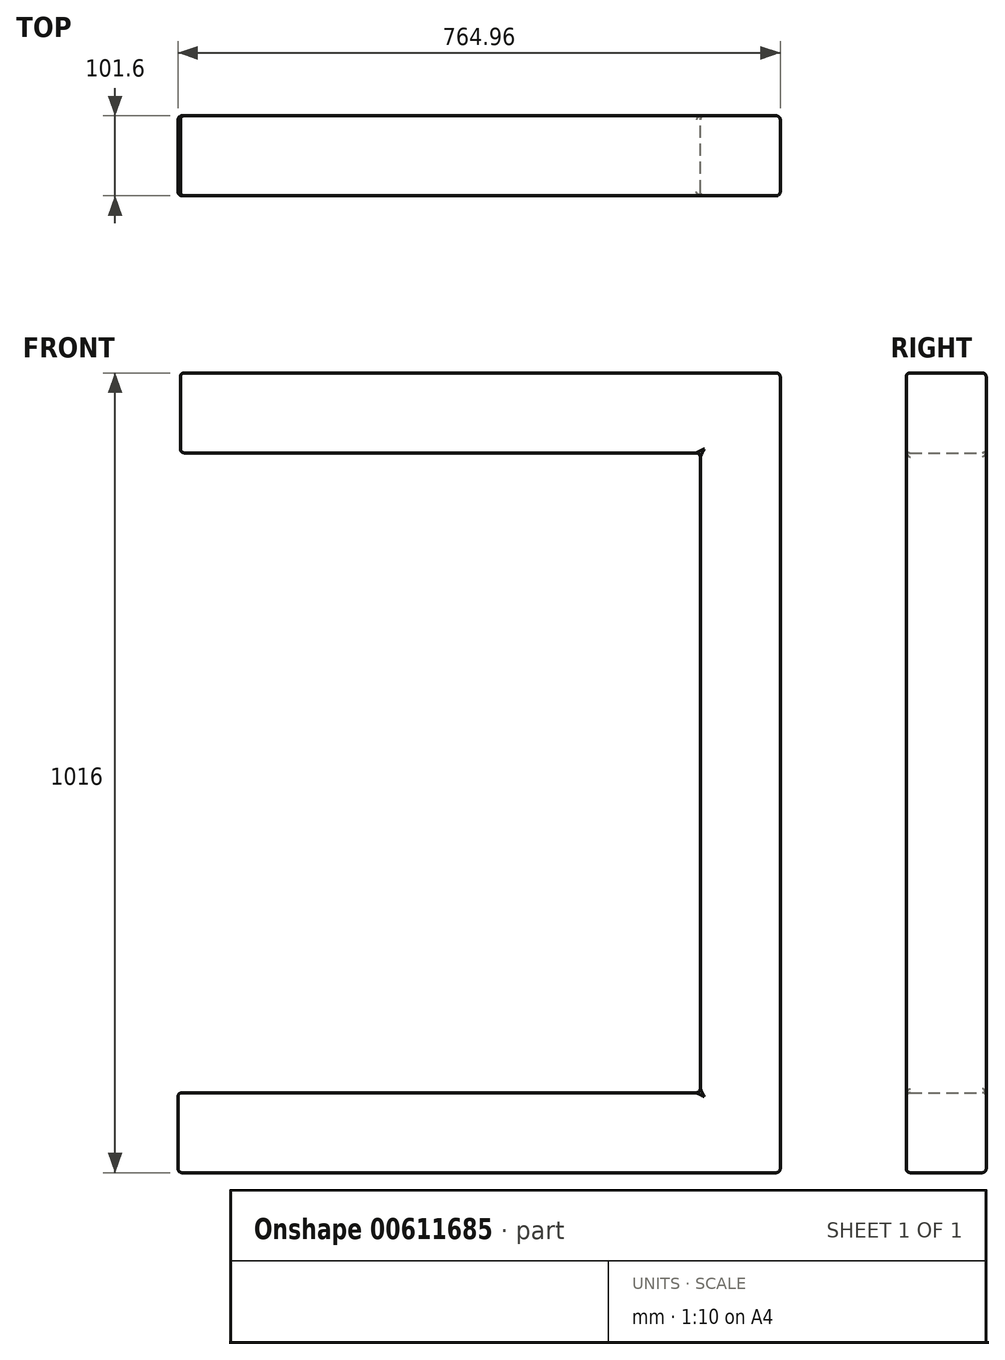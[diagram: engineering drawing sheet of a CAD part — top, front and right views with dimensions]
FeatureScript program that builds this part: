
annotation { "Feature Type Name" : "Feature", "Feature Type Description" : "" }
export const myFeature = defineFeature(function(context is Context, id is Id, definition is map)
    precondition{}
    {
        {
            var Q0;
            Q0=qCreatedBy(makeId("Front.planeOp"),FACE);
            var sketch = newSketch(context, id + "F0", { "sketchPlane" : qUnion([Q0])});
            skLineSegment(sketch, "E0.bottom", {"start": v(-441.4, 413.34) * mm, "end": v(219, 413.34) * mm});
            skLineSegment(sketch, "E0.top", {"start": v(-441.4, 311.74) * mm, "end": v(219, 311.74) * mm});
            skLineSegment(sketch, "E0.left", {"start": v(-441.4, 413.34) * mm, "end": v(-441.4, 311.74) * mm});
            skLineSegment(sketch, "E0.right", {"start": v(219, 413.34) * mm, "end": v(219, 311.74) * mm});
            skLineSegment(sketch, "E1.bottom", {"start": v(219, 413.34) * mm, "end": v(320.6, 413.34) * mm});
            skLineSegment(sketch, "E1.top", {"start": v(219, -602.66) * mm, "end": v(320.6, -602.66) * mm});
            skLineSegment(sketch, "E1.left", {"start": v(219, 413.34) * mm, "end": v(219, -602.66) * mm});
            skLineSegment(sketch, "E1.right", {"start": v(320.6, 413.34) * mm, "end": v(320.6, -602.66) * mm});
            skLineSegment(sketch, "E2.bottom", {"start": v(-444.37, -501.06) * mm, "end": v(219, -501.06) * mm});
            skLineSegment(sketch, "E2.top", {"start": v(-444.37, -602.66) * mm, "end": v(219, -602.66) * mm});
            skLineSegment(sketch, "E2.left", {"start": v(-444.37, -501.06) * mm, "end": v(-444.37, -602.66) * mm});
            skLineSegment(sketch, "E2.right", {"start": v(219, -501.06) * mm, "end": v(219, -602.66) * mm});
            skSolve(sketch);
        }
        {
            var Q0;
            Q0=makeQuery(id+"F0.imprint","IMPRINT",FACE,{"disambiguationData":[TD([[makeQuery(id+"F0.imprint","IMPRINT",EDGE,{"derivedFrom":sQuery(id+"F0.wireOp",EDGE,"E2.bottom")}),-1.0]])]});
            var Q1;
            {var subQ3=sQuery(id+"F0.wireOp",EDGE,"E1.bottom");Q1=makeQuery(id+"F0.imprint","IMPRINT",FACE,{"disambiguationData":[TD([[makeQuery(id+"F0.imprint","IMPRINT",EDGE,{"derivedFrom":subQ3}),-1.0]])]});}
            var Q2;
            {var subQ0=sQuery(id+"F0.wireOp",EDGE,"E0.bottom");Q2=makeQuery(id+"F0.imprint","IMPRINT",FACE,{"disambiguationData":[TD([[makeQuery(id+"F0.imprint","IMPRINT",EDGE,{"derivedFrom":subQ0}),-1.0]])]});}
            extrude(context, id + "F1", {"entities" : qUnion([Q0, Q1, Q2]), "depth" : 101.6 * mm, "offsetDistance" : 25.4 * mm});
        }
        {
            var Q0;
            Q0=makeQuery(id+"F1.opExtrude","CAP_EDGE",EDGE,{"disambiguationData":[OSD([sQuery(id+"F0.wireOp",EDGE,"E0.bottom"),sQuery(id+"F0.wireOp",EDGE,"E1.bottom")])],"isStart":true});
            var Q1;
            Q1=makeQuery(id+"F1.opExtrude","CAP_EDGE",EDGE,{"disambiguationData":[OSD([sQuery(id+"F0.wireOp",EDGE,"E0.top")])],"isStart":true});
            var Q2;
            Q2=makeQuery(id+"F1.opExtrude","CAP_EDGE",EDGE,{"disambiguationData":[OSD([sQuery(id+"F0.wireOp",EDGE,"E0.left")])],"isStart":true});
            var Q3;
            Q3=makeQuery(id+"F1.opExtrude","CAP_EDGE",EDGE,{"disambiguationData":[OSD([sQuery(id+"F0.wireOp",EDGE,"E1.right")])],"isStart":true});
            var Q4;
            Q4=makeQuery(id+"F1.opExtrude","SWEPT_EDGE",EDGE,{"disambiguationData":[OSD([sQuery(id+"F0.wireOp",EDGE,"E1.bottom"),sQuery(id+"F0.wireOp",EDGE,"E1.right")])]});
            var Q5;
            Q5=makeQuery(id+"F1.opExtrude","CAP_EDGE",EDGE,{"disambiguationData":[OSD([sQuery(id+"F0.wireOp",EDGE,"E1.left")])],"isStart":true});
            var Q6;
            Q6=makeQuery(id+"F1.opExtrude","SWEPT_FACE",FACE,{"disambiguationData":[OSD([sQuery(id+"F0.wireOp",EDGE,"E1.right")])]});
            var Q7;
            Q7=makeQuery(id+"F1.opExtrude","CAP_EDGE",EDGE,{"disambiguationData":[OSD([sQuery(id+"F0.wireOp",EDGE,"E2.bottom")])],"isStart":true});
            var Q8;
            Q8=makeQuery(id+"F1.opExtrude","CAP_EDGE",EDGE,{"disambiguationData":[OSD([sQuery(id+"F0.wireOp",EDGE,"E1.top"),sQuery(id+"F0.wireOp",EDGE,"E2.top")])],"isStart":true});
            var Q9;
            Q9=makeQuery(id+"F1.opExtrude","CAP_EDGE",EDGE,{"disambiguationData":[OSD([sQuery(id+"F0.wireOp",EDGE,"E2.left")])],"isStart":true});
            var Q10;
            Q10=makeQuery(id+"F1.opExtrude","SWEPT_EDGE",EDGE,{"disambiguationData":[OSD([sQuery(id+"F0.wireOp",EDGE,"E0.top"),sQuery(id+"F0.wireOp",EDGE,"E0.left")])]});
            var Q11;
            Q11=makeQuery(id+"F1.opExtrude","SWEPT_EDGE",EDGE,{"disambiguationData":[OSD([sQuery(id+"F0.wireOp",EDGE,"E2.bottom"),sQuery(id+"F0.wireOp",EDGE,"E2.left")])]});
            var Q12;
            Q12=makeQuery(id+"F1.opExtrude","SWEPT_EDGE",EDGE,{"disambiguationData":[OSD([sQuery(id+"F0.wireOp",EDGE,"E2.top"),sQuery(id+"F0.wireOp",EDGE,"E2.left")])]});
            var Q13;
            Q13=makeQuery(id+"F1.opExtrude","SWEPT_EDGE",EDGE,{"disambiguationData":[OSD([sQuery(id+"F0.wireOp",EDGE,"E2.bottom"),sQuery(id+"F0.wireOp",EDGE,"E2.left")])]});
            fillet(context, id + "F2", {"entities" : qUnion([Q0, Q1, Q2, Q3, Q4, Q5, Q6, Q7, Q8, Q9, Q10, Q11, Q12, Q13]), "radius" : 5.08 * mm, "tangentPropagation" : true, "allowEdgeOverflow" : false});
        }
        {
            var Q0;
            Q0=makeQuery(id+"F1.opExtrude","CAP_EDGE",EDGE,{"disambiguationData":[OSD([sQuery(id+"F0.wireOp",EDGE,"E0.top")])],"isStart":false});
            var Q1;
            Q1=makeQuery(id+"F1.opExtrude","CAP_EDGE",EDGE,{"disambiguationData":[OSD([sQuery(id+"F0.wireOp",EDGE,"E0.bottom"),sQuery(id+"F0.wireOp",EDGE,"E1.bottom")])],"isStart":false});
            var Q2;
            Q2=makeQuery(id+"F1.opExtrude","CAP_EDGE",EDGE,{"disambiguationData":[OSD([sQuery(id+"F0.wireOp",EDGE,"E1.left")])],"isStart":false});
            var Q3;
            Q3=makeQuery(id+"F1.opExtrude","CAP_EDGE",EDGE,{"disambiguationData":[OSD([sQuery(id+"F0.wireOp",EDGE,"E0.left")])],"isStart":false});
            var Q4;
            Q4=makeQuery(id+"F1.opExtrude","CAP_EDGE",EDGE,{"disambiguationData":[OSD([sQuery(id+"F0.wireOp",EDGE,"E2.bottom")])],"isStart":false});
            var Q5;
            Q5=makeQuery(id+"F1.opExtrude","CAP_EDGE",EDGE,{"disambiguationData":[OSD([sQuery(id+"F0.wireOp",EDGE,"E2.left")])],"isStart":false});
            var Q6;
            Q6=makeQuery(id+"F1.opExtrude","CAP_EDGE",EDGE,{"disambiguationData":[OSD([sQuery(id+"F0.wireOp",EDGE,"E1.top"),sQuery(id+"F0.wireOp",EDGE,"E2.top")])],"isStart":false});
            var Q7;
            {var subQ0=sQuery(id+"F0.wireOp",EDGE,"E1.right");Q7=makeQuery(id+"F2.opFillet","BLEND_EDGE",EDGE,{"blendedFrom":[makeQuery(id+"F1.opExtrude","CAP_EDGE",EDGE,{"disambiguationData":[OSD([subQ0])],"isStart":false}),makeQuery(id+"F1.opExtrude","CAP_FACE",FACE,{"disambiguationData":[OSD([sQuery(id+"F0.wireOp",EDGE,"E0.bottom"),sQuery(id+"F0.wireOp",EDGE,"E0.top"),sQuery(id+"F0.wireOp",EDGE,"E0.left"),sQuery(id+"F0.wireOp",EDGE,"E1.bottom"),sQuery(id+"F0.wireOp",EDGE,"E1.top"),sQuery(id+"F0.wireOp",EDGE,"E1.left"),subQ0,sQuery(id+"F0.wireOp",EDGE,"E2.bottom"),sQuery(id+"F0.wireOp",EDGE,"E2.top"),sQuery(id+"F0.wireOp",EDGE,"E2.left")])],"isStart":false})],"blendedInto":[makeQuery(id+"F1.opExtrude","CAP_FACE",FACE,{"disambiguationData":[OSD([sQuery(id+"F0.wireOp",EDGE,"E0.bottom"),sQuery(id+"F0.wireOp",EDGE,"E0.top"),sQuery(id+"F0.wireOp",EDGE,"E0.left"),sQuery(id+"F0.wireOp",EDGE,"E1.bottom"),sQuery(id+"F0.wireOp",EDGE,"E1.top"),sQuery(id+"F0.wireOp",EDGE,"E1.left"),subQ0,sQuery(id+"F0.wireOp",EDGE,"E2.bottom"),sQuery(id+"F0.wireOp",EDGE,"E2.top"),sQuery(id+"F0.wireOp",EDGE,"E2.left")])],"isStart":false})]});}
            fillet(context, id + "F3", {"entities" : qUnion([Q0, Q1, Q2, Q3, Q4, Q5, Q6, Q7]), "radius" : 5.08 * mm, "tangentPropagation" : true, "allowEdgeOverflow" : false});
        }
        {
            var Q0;
            {var subQ0=sQuery(id+"F0.wireOp",EDGE,"E1.right");Q0=makeQuery(id+"F2.opFillet","BLEND_EDGE",EDGE,{"blendedFrom":[makeQuery(id+"F1.opExtrude","CAP_EDGE",EDGE,{"disambiguationData":[OSD([subQ0])],"isStart":false}),makeQuery(id+"F1.opExtrude","SWEPT_FACE",FACE,{"disambiguationData":[OSD([subQ0])]})],"blendedInto":[makeQuery(id+"F1.opExtrude","SWEPT_FACE",FACE,{"disambiguationData":[OSD([subQ0])]})]});}
            var Q1;
            Q1=makeQuery(id+"F3.opFillet","BLEND_EDGE",EDGE,{"blendedFrom":[makeQuery(id+"F1.opExtrude","CAP_EDGE",EDGE,{"disambiguationData":[OSD([sQuery(id+"F0.wireOp",EDGE,"E1.left")])],"isStart":false}),makeQuery(id+"F1.opExtrude","CAP_EDGE",EDGE,{"disambiguationData":[OSD([sQuery(id+"F0.wireOp",EDGE,"E2.bottom")])],"isStart":false})],"blendedInto":[]});
            var Q2;
            {var subQ0=sQuery(id+"F0.wireOp",EDGE,"E1.left");Q2=makeQuery(id+"F3.opFillet","BLEND_EDGE",EDGE,{"blendedFrom":[makeQuery(id+"F1.opExtrude","CAP_EDGE",EDGE,{"disambiguationData":[OSD([subQ0])],"isStart":false}),makeQuery(id+"F1.opExtrude","CAP_FACE",FACE,{"disambiguationData":[OSD([sQuery(id+"F0.wireOp",EDGE,"E0.bottom"),sQuery(id+"F0.wireOp",EDGE,"E0.top"),sQuery(id+"F0.wireOp",EDGE,"E0.left"),sQuery(id+"F0.wireOp",EDGE,"E1.bottom"),sQuery(id+"F0.wireOp",EDGE,"E1.top"),subQ0,sQuery(id+"F0.wireOp",EDGE,"E1.right"),sQuery(id+"F0.wireOp",EDGE,"E2.bottom"),sQuery(id+"F0.wireOp",EDGE,"E2.top"),sQuery(id+"F0.wireOp",EDGE,"E2.left")])],"isStart":false})],"blendedInto":[makeQuery(id+"F1.opExtrude","CAP_FACE",FACE,{"disambiguationData":[OSD([sQuery(id+"F0.wireOp",EDGE,"E0.bottom"),sQuery(id+"F0.wireOp",EDGE,"E0.top"),sQuery(id+"F0.wireOp",EDGE,"E0.left"),sQuery(id+"F0.wireOp",EDGE,"E1.bottom"),sQuery(id+"F0.wireOp",EDGE,"E1.top"),subQ0,sQuery(id+"F0.wireOp",EDGE,"E1.right"),sQuery(id+"F0.wireOp",EDGE,"E2.bottom"),sQuery(id+"F0.wireOp",EDGE,"E2.top"),sQuery(id+"F0.wireOp",EDGE,"E2.left")])],"isStart":false})]});}
            var Q3;
            {var subQ0=sQuery(id+"F0.wireOp",EDGE,"E1.left");Q3=makeQuery(id+"F3.opFillet","BLEND_EDGE",EDGE,{"blendedFrom":[makeQuery(id+"F1.opExtrude","CAP_EDGE",EDGE,{"disambiguationData":[OSD([subQ0])],"isStart":false}),makeQuery(id+"F1.opExtrude","SWEPT_FACE",FACE,{"disambiguationData":[OSD([subQ0])]})],"blendedInto":[makeQuery(id+"F1.opExtrude","SWEPT_FACE",FACE,{"disambiguationData":[OSD([subQ0])]})]});}
            var Q4;
            {var subQ0=sQuery(id+"F0.wireOp",EDGE,"E2.top");var subQ1=sQuery(id+"F0.wireOp",EDGE,"E1.top");Q4=makeQuery(id+"F3.opFillet","BLEND_EDGE",EDGE,{"blendedFrom":[makeQuery(id+"F1.opExtrude","CAP_EDGE",EDGE,{"disambiguationData":[OSD([subQ1,subQ0])],"isStart":false}),makeQuery(id+"F1.opExtrude","CAP_FACE",FACE,{"disambiguationData":[OSD([sQuery(id+"F0.wireOp",EDGE,"E0.bottom"),sQuery(id+"F0.wireOp",EDGE,"E0.top"),sQuery(id+"F0.wireOp",EDGE,"E0.left"),sQuery(id+"F0.wireOp",EDGE,"E1.bottom"),subQ1,sQuery(id+"F0.wireOp",EDGE,"E1.left"),sQuery(id+"F0.wireOp",EDGE,"E1.right"),sQuery(id+"F0.wireOp",EDGE,"E2.bottom"),subQ0,sQuery(id+"F0.wireOp",EDGE,"E2.left")])],"isStart":false})],"blendedInto":[makeQuery(id+"F1.opExtrude","CAP_FACE",FACE,{"disambiguationData":[OSD([sQuery(id+"F0.wireOp",EDGE,"E0.bottom"),sQuery(id+"F0.wireOp",EDGE,"E0.top"),sQuery(id+"F0.wireOp",EDGE,"E0.left"),sQuery(id+"F0.wireOp",EDGE,"E1.bottom"),subQ1,sQuery(id+"F0.wireOp",EDGE,"E1.left"),sQuery(id+"F0.wireOp",EDGE,"E1.right"),sQuery(id+"F0.wireOp",EDGE,"E2.bottom"),subQ0,sQuery(id+"F0.wireOp",EDGE,"E2.left")])],"isStart":false})]});}
            var Q5;
            {var subQ0=sQuery(id+"F0.wireOp",EDGE,"E1.right");Q5=makeQuery(id+"F2.opFillet","BLEND_EDGE",EDGE,{"blendedFrom":[makeQuery(id+"F1.opExtrude","CAP_EDGE",EDGE,{"disambiguationData":[OSD([subQ0])],"isStart":false}),makeQuery(id+"F1.opExtrude","CAP_FACE",FACE,{"disambiguationData":[OSD([sQuery(id+"F0.wireOp",EDGE,"E0.bottom"),sQuery(id+"F0.wireOp",EDGE,"E0.top"),sQuery(id+"F0.wireOp",EDGE,"E0.left"),sQuery(id+"F0.wireOp",EDGE,"E1.bottom"),sQuery(id+"F0.wireOp",EDGE,"E1.top"),sQuery(id+"F0.wireOp",EDGE,"E1.left"),subQ0,sQuery(id+"F0.wireOp",EDGE,"E2.bottom"),sQuery(id+"F0.wireOp",EDGE,"E2.top"),sQuery(id+"F0.wireOp",EDGE,"E2.left")])],"isStart":false})],"blendedInto":[makeQuery(id+"F1.opExtrude","CAP_FACE",FACE,{"disambiguationData":[OSD([sQuery(id+"F0.wireOp",EDGE,"E0.bottom"),sQuery(id+"F0.wireOp",EDGE,"E0.top"),sQuery(id+"F0.wireOp",EDGE,"E0.left"),sQuery(id+"F0.wireOp",EDGE,"E1.bottom"),sQuery(id+"F0.wireOp",EDGE,"E1.top"),sQuery(id+"F0.wireOp",EDGE,"E1.left"),subQ0,sQuery(id+"F0.wireOp",EDGE,"E2.bottom"),sQuery(id+"F0.wireOp",EDGE,"E2.top"),sQuery(id+"F0.wireOp",EDGE,"E2.left")])],"isStart":false})]});}
            var Q6;
            {var subQ0=sQuery(id+"F0.wireOp",EDGE,"E2.bottom");Q6=makeQuery(id+"F3.opFillet","BLEND_EDGE",EDGE,{"blendedFrom":[makeQuery(id+"F1.opExtrude","CAP_EDGE",EDGE,{"disambiguationData":[OSD([subQ0])],"isStart":false}),makeQuery(id+"F1.opExtrude","CAP_FACE",FACE,{"disambiguationData":[OSD([sQuery(id+"F0.wireOp",EDGE,"E0.bottom"),sQuery(id+"F0.wireOp",EDGE,"E0.top"),sQuery(id+"F0.wireOp",EDGE,"E0.left"),sQuery(id+"F0.wireOp",EDGE,"E1.bottom"),sQuery(id+"F0.wireOp",EDGE,"E1.top"),sQuery(id+"F0.wireOp",EDGE,"E1.left"),sQuery(id+"F0.wireOp",EDGE,"E1.right"),subQ0,sQuery(id+"F0.wireOp",EDGE,"E2.top"),sQuery(id+"F0.wireOp",EDGE,"E2.left")])],"isStart":false})],"blendedInto":[makeQuery(id+"F1.opExtrude","CAP_FACE",FACE,{"disambiguationData":[OSD([sQuery(id+"F0.wireOp",EDGE,"E0.bottom"),sQuery(id+"F0.wireOp",EDGE,"E0.top"),sQuery(id+"F0.wireOp",EDGE,"E0.left"),sQuery(id+"F0.wireOp",EDGE,"E1.bottom"),sQuery(id+"F0.wireOp",EDGE,"E1.top"),sQuery(id+"F0.wireOp",EDGE,"E1.left"),sQuery(id+"F0.wireOp",EDGE,"E1.right"),subQ0,sQuery(id+"F0.wireOp",EDGE,"E2.top"),sQuery(id+"F0.wireOp",EDGE,"E2.left")])],"isStart":false})]});}
            var Q7;
            {var subQ0=sQuery(id+"F0.wireOp",EDGE,"E1.right");Q7=makeQuery(id+"F2.opFillet","BLEND_EDGE",EDGE,{"blendedFrom":[makeQuery(id+"F1.opExtrude","SWEPT_EDGE",EDGE,{"disambiguationData":[OSD([sQuery(id+"F0.wireOp",EDGE,"E1.top"),subQ0])]}),makeQuery(id+"F1.opExtrude","CAP_EDGE",EDGE,{"disambiguationData":[OSD([subQ0])],"isStart":false})],"blendedInto":[]});}
            var Q8;
            {var subQ0=sQuery(id+"F0.wireOp",EDGE,"E2.bottom");Q8=makeQuery(id+"F3.opFillet","BLEND_EDGE",EDGE,{"blendedFrom":[makeQuery(id+"F1.opExtrude","CAP_EDGE",EDGE,{"disambiguationData":[OSD([subQ0])],"isStart":false}),makeQuery(id+"F1.opExtrude","SWEPT_FACE",FACE,{"disambiguationData":[OSD([subQ0])]})],"blendedInto":[makeQuery(id+"F1.opExtrude","SWEPT_FACE",FACE,{"disambiguationData":[OSD([subQ0])]})]});}
            var Q9;
            {var subQ0=sQuery(id+"F0.wireOp",EDGE,"E1.right");Q9=makeQuery(id+"F2.opFillet","BLEND_EDGE",EDGE,{"blendedFrom":[makeQuery(id+"F1.opExtrude","SWEPT_EDGE",EDGE,{"disambiguationData":[OSD([sQuery(id+"F0.wireOp",EDGE,"E1.top"),subQ0])]}),makeQuery(id+"F1.opExtrude","SWEPT_FACE",FACE,{"disambiguationData":[OSD([subQ0])]})],"blendedInto":[makeQuery(id+"F1.opExtrude","SWEPT_FACE",FACE,{"disambiguationData":[OSD([subQ0])]})]});}
            var Q10;
            {var subQ0=sQuery(id+"F0.wireOp",EDGE,"E1.right");Q10=makeQuery(id+"F3.opFillet","BLEND_EDGE",EDGE,{"blendedFrom":[makeQuery(id+"F1.opExtrude","CAP_EDGE",EDGE,{"disambiguationData":[OSD([sQuery(id+"F0.wireOp",EDGE,"E1.top"),sQuery(id+"F0.wireOp",EDGE,"E2.top")])],"isStart":false}),makeQuery(id+"F2.opFillet","BLEND_FACE",FACE,{"disambiguationData":[OSD([subQ0]),TDD([makeQuery(id+"F1.opExtrude","CAP_EDGE",EDGE,{"disambiguationData":[OSD([subQ0])],"isStart":false})])]})],"blendedInto":[makeQuery(id+"F2.opFillet","BLEND_FACE",FACE,{"disambiguationData":[OSD([subQ0]),TDD([makeQuery(id+"F1.opExtrude","CAP_EDGE",EDGE,{"disambiguationData":[OSD([subQ0])],"isStart":false})])]})]});}
            var Q11;
            {var subQ0=sQuery(id+"F0.wireOp",EDGE,"E2.top");var subQ1=sQuery(id+"F0.wireOp",EDGE,"E1.top");Q11=makeQuery(id+"F3.opFillet","BLEND_EDGE",EDGE,{"blendedFrom":[makeQuery(id+"F1.opExtrude","CAP_EDGE",EDGE,{"disambiguationData":[OSD([subQ1,subQ0])],"isStart":false}),makeQuery(id+"F1.opExtrude","SWEPT_FACE",FACE,{"disambiguationData":[OSD([subQ1,subQ0])]})],"blendedInto":[makeQuery(id+"F1.opExtrude","SWEPT_FACE",FACE,{"disambiguationData":[OSD([subQ1,subQ0])]})]});}
            var Q12;
            {var subQ0=sQuery(id+"F0.wireOp",EDGE,"E1.right");Q12=makeQuery(id+"F2.opFillet","BLEND_EDGE",EDGE,{"blendedFrom":[makeQuery(id+"F1.opExtrude","CAP_EDGE",EDGE,{"disambiguationData":[OSD([subQ0])],"isStart":true}),makeQuery(id+"F1.opExtrude","CAP_FACE",FACE,{"disambiguationData":[OSD([sQuery(id+"F0.wireOp",EDGE,"E0.bottom"),sQuery(id+"F0.wireOp",EDGE,"E0.top"),sQuery(id+"F0.wireOp",EDGE,"E0.left"),sQuery(id+"F0.wireOp",EDGE,"E1.bottom"),sQuery(id+"F0.wireOp",EDGE,"E1.top"),sQuery(id+"F0.wireOp",EDGE,"E1.left"),subQ0,sQuery(id+"F0.wireOp",EDGE,"E2.bottom"),sQuery(id+"F0.wireOp",EDGE,"E2.top"),sQuery(id+"F0.wireOp",EDGE,"E2.left")])],"isStart":true})],"blendedInto":[makeQuery(id+"F1.opExtrude","CAP_FACE",FACE,{"disambiguationData":[OSD([sQuery(id+"F0.wireOp",EDGE,"E0.bottom"),sQuery(id+"F0.wireOp",EDGE,"E0.top"),sQuery(id+"F0.wireOp",EDGE,"E0.left"),sQuery(id+"F0.wireOp",EDGE,"E1.bottom"),sQuery(id+"F0.wireOp",EDGE,"E1.top"),sQuery(id+"F0.wireOp",EDGE,"E1.left"),subQ0,sQuery(id+"F0.wireOp",EDGE,"E2.bottom"),sQuery(id+"F0.wireOp",EDGE,"E2.top"),sQuery(id+"F0.wireOp",EDGE,"E2.left")])],"isStart":true})]});}
            var Q13;
            {var subQ0=sQuery(id+"F0.wireOp",EDGE,"E1.right");Q13=makeQuery(id+"F2.opFillet","BLEND_EDGE",EDGE,{"blendedFrom":[makeQuery(id+"F1.opExtrude","CAP_EDGE",EDGE,{"disambiguationData":[OSD([subQ0])],"isStart":true}),makeQuery(id+"F1.opExtrude","SWEPT_FACE",FACE,{"disambiguationData":[OSD([subQ0])]})],"blendedInto":[makeQuery(id+"F1.opExtrude","SWEPT_FACE",FACE,{"disambiguationData":[OSD([subQ0])]})]});}
            var Q14;
            {var subQ0=sQuery(id+"F0.wireOp",EDGE,"E2.bottom");Q14=makeQuery(id+"F2.opFillet","BLEND_EDGE",EDGE,{"blendedFrom":[makeQuery(id+"F1.opExtrude","CAP_EDGE",EDGE,{"disambiguationData":[OSD([subQ0])],"isStart":true}),makeQuery(id+"F1.opExtrude","CAP_FACE",FACE,{"disambiguationData":[OSD([sQuery(id+"F0.wireOp",EDGE,"E0.bottom"),sQuery(id+"F0.wireOp",EDGE,"E0.top"),sQuery(id+"F0.wireOp",EDGE,"E0.left"),sQuery(id+"F0.wireOp",EDGE,"E1.bottom"),sQuery(id+"F0.wireOp",EDGE,"E1.top"),sQuery(id+"F0.wireOp",EDGE,"E1.left"),sQuery(id+"F0.wireOp",EDGE,"E1.right"),subQ0,sQuery(id+"F0.wireOp",EDGE,"E2.top"),sQuery(id+"F0.wireOp",EDGE,"E2.left")])],"isStart":true})],"blendedInto":[makeQuery(id+"F1.opExtrude","CAP_FACE",FACE,{"disambiguationData":[OSD([sQuery(id+"F0.wireOp",EDGE,"E0.bottom"),sQuery(id+"F0.wireOp",EDGE,"E0.top"),sQuery(id+"F0.wireOp",EDGE,"E0.left"),sQuery(id+"F0.wireOp",EDGE,"E1.bottom"),sQuery(id+"F0.wireOp",EDGE,"E1.top"),sQuery(id+"F0.wireOp",EDGE,"E1.left"),sQuery(id+"F0.wireOp",EDGE,"E1.right"),subQ0,sQuery(id+"F0.wireOp",EDGE,"E2.top"),sQuery(id+"F0.wireOp",EDGE,"E2.left")])],"isStart":true})]});}
            var Q15;
            {var subQ0=sQuery(id+"F0.wireOp",EDGE,"E2.bottom");Q15=makeQuery(id+"F2.opFillet","BLEND_EDGE",EDGE,{"blendedFrom":[makeQuery(id+"F1.opExtrude","CAP_EDGE",EDGE,{"disambiguationData":[OSD([subQ0])],"isStart":true}),makeQuery(id+"F1.opExtrude","SWEPT_FACE",FACE,{"disambiguationData":[OSD([subQ0])]})],"blendedInto":[makeQuery(id+"F1.opExtrude","SWEPT_FACE",FACE,{"disambiguationData":[OSD([subQ0])]})]});}
            var Q16;
            Q16=makeQuery(id+"F2.opFillet","BLEND_EDGE",EDGE,{"blendedFrom":[makeQuery(id+"F1.opExtrude","CAP_EDGE",EDGE,{"disambiguationData":[OSD([sQuery(id+"F0.wireOp",EDGE,"E1.left")])],"isStart":true}),makeQuery(id+"F1.opExtrude","CAP_EDGE",EDGE,{"disambiguationData":[OSD([sQuery(id+"F0.wireOp",EDGE,"E2.bottom")])],"isStart":true})],"blendedInto":[]});
            var Q17;
            {var subQ0=sQuery(id+"F0.wireOp",EDGE,"E1.left");Q17=makeQuery(id+"F2.opFillet","BLEND_EDGE",EDGE,{"blendedFrom":[makeQuery(id+"F1.opExtrude","CAP_EDGE",EDGE,{"disambiguationData":[OSD([subQ0])],"isStart":true}),makeQuery(id+"F1.opExtrude","CAP_FACE",FACE,{"disambiguationData":[OSD([sQuery(id+"F0.wireOp",EDGE,"E0.bottom"),sQuery(id+"F0.wireOp",EDGE,"E0.top"),sQuery(id+"F0.wireOp",EDGE,"E0.left"),sQuery(id+"F0.wireOp",EDGE,"E1.bottom"),sQuery(id+"F0.wireOp",EDGE,"E1.top"),subQ0,sQuery(id+"F0.wireOp",EDGE,"E1.right"),sQuery(id+"F0.wireOp",EDGE,"E2.bottom"),sQuery(id+"F0.wireOp",EDGE,"E2.top"),sQuery(id+"F0.wireOp",EDGE,"E2.left")])],"isStart":true})],"blendedInto":[makeQuery(id+"F1.opExtrude","CAP_FACE",FACE,{"disambiguationData":[OSD([sQuery(id+"F0.wireOp",EDGE,"E0.bottom"),sQuery(id+"F0.wireOp",EDGE,"E0.top"),sQuery(id+"F0.wireOp",EDGE,"E0.left"),sQuery(id+"F0.wireOp",EDGE,"E1.bottom"),sQuery(id+"F0.wireOp",EDGE,"E1.top"),subQ0,sQuery(id+"F0.wireOp",EDGE,"E1.right"),sQuery(id+"F0.wireOp",EDGE,"E2.bottom"),sQuery(id+"F0.wireOp",EDGE,"E2.top"),sQuery(id+"F0.wireOp",EDGE,"E2.left")])],"isStart":true})]});}
            var Q18;
            {var subQ0=sQuery(id+"F0.wireOp",EDGE,"E1.left");Q18=makeQuery(id+"F2.opFillet","BLEND_EDGE",EDGE,{"blendedFrom":[makeQuery(id+"F1.opExtrude","CAP_EDGE",EDGE,{"disambiguationData":[OSD([subQ0])],"isStart":true}),makeQuery(id+"F1.opExtrude","SWEPT_FACE",FACE,{"disambiguationData":[OSD([subQ0])]})],"blendedInto":[makeQuery(id+"F1.opExtrude","SWEPT_FACE",FACE,{"disambiguationData":[OSD([subQ0])]})]});}
            var Q19;
            Q19=makeQuery(id+"F1.opExtrude","SWEPT_EDGE",EDGE,{"disambiguationData":[OSD([sQuery(id+"F0.wireOp",EDGE,"E1.left"),sQuery(id+"F0.wireOp",EDGE,"E2.bottom"),sQuery(id+"F0.wireOp",EDGE,"E2.right")])]});
            var Q20;
            {var subQ0=sQuery(id+"F0.wireOp",EDGE,"E1.right");var subQ1=sQuery(id+"F0.wireOp",EDGE,"E1.top");Q20=makeQuery(id+"F3.opFillet","BLEND_EDGE",EDGE,{"blendedFrom":[makeQuery(id+"F1.opExtrude","CAP_EDGE",EDGE,{"disambiguationData":[OSD([subQ1,sQuery(id+"F0.wireOp",EDGE,"E2.top")])],"isStart":false}),makeQuery(id+"F2.opFillet","BLEND_FACE",FACE,{"disambiguationData":[OSD([subQ1,subQ0]),TDD([makeQuery(id+"F1.opExtrude","SWEPT_EDGE",EDGE,{"disambiguationData":[OSD([subQ1,subQ0])]})])]})],"blendedInto":[makeQuery(id+"F2.opFillet","BLEND_FACE",FACE,{"disambiguationData":[OSD([subQ1,subQ0]),TDD([makeQuery(id+"F1.opExtrude","SWEPT_EDGE",EDGE,{"disambiguationData":[OSD([subQ1,subQ0])]})])]})]});}
            var Q21;
            {var subQ0=sQuery(id+"F0.wireOp",EDGE,"E1.right");var subQ1=sQuery(id+"F0.wireOp",EDGE,"E1.top");Q21=makeQuery(id+"F2.opFillet","BLEND_EDGE",EDGE,{"blendedFrom":[makeQuery(id+"F1.opExtrude","CAP_VERTEX",VERTEX,{"disambiguationData":[OSD([subQ1,subQ0])],"isStart":true}),makeQuery(id+"F1.opExtrude","SWEPT_EDGE",EDGE,{"disambiguationData":[OSD([subQ1,subQ0])]})],"blendedInto":[]});}
            var Q22;
            {var subQ0=sQuery(id+"F0.wireOp",EDGE,"E1.top");Q22=makeQuery(id+"F2.opFillet","BLEND_EDGE",EDGE,{"blendedFrom":[makeQuery(id+"F1.opExtrude","SWEPT_EDGE",EDGE,{"disambiguationData":[OSD([subQ0,sQuery(id+"F0.wireOp",EDGE,"E1.right")])]}),makeQuery(id+"F1.opExtrude","SWEPT_FACE",FACE,{"disambiguationData":[OSD([subQ0,sQuery(id+"F0.wireOp",EDGE,"E2.top")])]})],"blendedInto":[makeQuery(id+"F1.opExtrude","SWEPT_FACE",FACE,{"disambiguationData":[OSD([subQ0,sQuery(id+"F0.wireOp",EDGE,"E2.top")])]})]});}
            var Q23;
            {var subQ0=sQuery(id+"F0.wireOp",EDGE,"E1.right");Q23=makeQuery(id+"F2.opFillet","BLEND_EDGE",EDGE,{"blendedFrom":[makeQuery(id+"F1.opExtrude","CAP_VERTEX",VERTEX,{"disambiguationData":[OSD([sQuery(id+"F0.wireOp",EDGE,"E1.top"),subQ0])],"isStart":true}),makeQuery(id+"F1.opExtrude","CAP_EDGE",EDGE,{"disambiguationData":[OSD([subQ0])],"isStart":true})],"blendedInto":[]});}
            var Q24;
            {var subQ0=sQuery(id+"F0.wireOp",EDGE,"E1.top");Q24=makeQuery(id+"F2.opFillet","BLEND_EDGE",EDGE,{"blendedFrom":[makeQuery(id+"F1.opExtrude","CAP_VERTEX",VERTEX,{"disambiguationData":[OSD([subQ0,sQuery(id+"F0.wireOp",EDGE,"E1.right")])],"isStart":true}),makeQuery(id+"F1.opExtrude","CAP_EDGE",EDGE,{"disambiguationData":[OSD([subQ0,sQuery(id+"F0.wireOp",EDGE,"E2.top")])],"isStart":true})],"blendedInto":[]});}
            var Q25;
            {var subQ0=sQuery(id+"F0.wireOp",EDGE,"E2.top");var subQ1=sQuery(id+"F0.wireOp",EDGE,"E1.top");Q25=makeQuery(id+"F2.opFillet","BLEND_EDGE",EDGE,{"blendedFrom":[makeQuery(id+"F1.opExtrude","CAP_EDGE",EDGE,{"disambiguationData":[OSD([subQ1,subQ0])],"isStart":true}),makeQuery(id+"F1.opExtrude","SWEPT_FACE",FACE,{"disambiguationData":[OSD([subQ1,subQ0])]})],"blendedInto":[makeQuery(id+"F1.opExtrude","SWEPT_FACE",FACE,{"disambiguationData":[OSD([subQ1,subQ0])]})]});}
            var Q26;
            {var subQ0=sQuery(id+"F0.wireOp",EDGE,"E2.top");var subQ1=sQuery(id+"F0.wireOp",EDGE,"E1.top");Q26=makeQuery(id+"F2.opFillet","BLEND_EDGE",EDGE,{"blendedFrom":[makeQuery(id+"F1.opExtrude","CAP_EDGE",EDGE,{"disambiguationData":[OSD([subQ1,subQ0])],"isStart":true}),makeQuery(id+"F1.opExtrude","CAP_FACE",FACE,{"disambiguationData":[OSD([sQuery(id+"F0.wireOp",EDGE,"E0.bottom"),sQuery(id+"F0.wireOp",EDGE,"E0.top"),sQuery(id+"F0.wireOp",EDGE,"E0.left"),sQuery(id+"F0.wireOp",EDGE,"E1.bottom"),subQ1,sQuery(id+"F0.wireOp",EDGE,"E1.left"),sQuery(id+"F0.wireOp",EDGE,"E1.right"),sQuery(id+"F0.wireOp",EDGE,"E2.bottom"),subQ0,sQuery(id+"F0.wireOp",EDGE,"E2.left")])],"isStart":true})],"blendedInto":[makeQuery(id+"F1.opExtrude","CAP_FACE",FACE,{"disambiguationData":[OSD([sQuery(id+"F0.wireOp",EDGE,"E0.bottom"),sQuery(id+"F0.wireOp",EDGE,"E0.top"),sQuery(id+"F0.wireOp",EDGE,"E0.left"),sQuery(id+"F0.wireOp",EDGE,"E1.bottom"),subQ1,sQuery(id+"F0.wireOp",EDGE,"E1.left"),sQuery(id+"F0.wireOp",EDGE,"E1.right"),sQuery(id+"F0.wireOp",EDGE,"E2.bottom"),subQ0,sQuery(id+"F0.wireOp",EDGE,"E2.left")])],"isStart":true})]});}
            var Q27;
            Q27=makeQuery(id+"F3.opFillet","BLEND_EDGE",EDGE,{"blendedFrom":[makeQuery(id+"F1.opExtrude","CAP_EDGE",EDGE,{"disambiguationData":[OSD([sQuery(id+"F0.wireOp",EDGE,"E1.left")])],"isStart":false}),makeQuery(id+"F1.opExtrude","CAP_EDGE",EDGE,{"disambiguationData":[OSD([sQuery(id+"F0.wireOp",EDGE,"E0.top")])],"isStart":false})],"blendedInto":[]});
            var Q28;
            {var subQ0=sQuery(id+"F0.wireOp",EDGE,"E2.bottom");var subQ1=sQuery(id+"F0.wireOp",EDGE,"E2.left");Q28=makeQuery(id+"F3.opFillet","BLEND_EDGE",EDGE,{"blendedFrom":[makeQuery(id+"F2.opFillet","BLEND_EDGE",EDGE,{"blendedFrom":[makeQuery(id+"F1.opExtrude","SWEPT_EDGE",EDGE,{"disambiguationData":[OSD([subQ0,subQ1])]}),makeQuery(id+"F1.opExtrude","CAP_FACE",FACE,{"disambiguationData":[OSD([sQuery(id+"F0.wireOp",EDGE,"E0.bottom"),sQuery(id+"F0.wireOp",EDGE,"E0.top"),sQuery(id+"F0.wireOp",EDGE,"E0.left"),sQuery(id+"F0.wireOp",EDGE,"E1.bottom"),sQuery(id+"F0.wireOp",EDGE,"E1.top"),sQuery(id+"F0.wireOp",EDGE,"E1.left"),sQuery(id+"F0.wireOp",EDGE,"E1.right"),subQ0,sQuery(id+"F0.wireOp",EDGE,"E2.top"),subQ1])],"isStart":false})],"blendedInto":[makeQuery(id+"F1.opExtrude","CAP_FACE",FACE,{"disambiguationData":[OSD([sQuery(id+"F0.wireOp",EDGE,"E0.bottom"),sQuery(id+"F0.wireOp",EDGE,"E0.top"),sQuery(id+"F0.wireOp",EDGE,"E0.left"),sQuery(id+"F0.wireOp",EDGE,"E1.bottom"),sQuery(id+"F0.wireOp",EDGE,"E1.top"),sQuery(id+"F0.wireOp",EDGE,"E1.left"),sQuery(id+"F0.wireOp",EDGE,"E1.right"),subQ0,sQuery(id+"F0.wireOp",EDGE,"E2.top"),subQ1])],"isStart":false})]}),makeQuery(id+"F1.opExtrude","CAP_EDGE",EDGE,{"disambiguationData":[OSD([subQ0])],"isStart":false})],"blendedInto":[]});}
            var Q29;
            {var subQ0=sQuery(id+"F0.wireOp",EDGE,"E0.left");var subQ1=sQuery(id+"F0.wireOp",EDGE,"E0.top");var subQ2=makeQuery(id+"F1.opExtrude","SWEPT_EDGE",EDGE,{"disambiguationData":[OSD([subQ1,subQ0])]});Q29=makeQuery(id+"F3.opFillet","BLEND_EDGE",EDGE,{"blendedFrom":[makeQuery(id+"F2.opFillet","BLEND_EDGE",EDGE,{"blendedFrom":[subQ2,makeQuery(id+"F1.opExtrude","CAP_FACE",FACE,{"disambiguationData":[OSD([sQuery(id+"F0.wireOp",EDGE,"E0.bottom"),subQ1,subQ0,sQuery(id+"F0.wireOp",EDGE,"E1.bottom"),sQuery(id+"F0.wireOp",EDGE,"E1.top"),sQuery(id+"F0.wireOp",EDGE,"E1.left"),sQuery(id+"F0.wireOp",EDGE,"E1.right"),sQuery(id+"F0.wireOp",EDGE,"E2.bottom"),sQuery(id+"F0.wireOp",EDGE,"E2.top"),sQuery(id+"F0.wireOp",EDGE,"E2.left")])],"isStart":false})],"blendedInto":[makeQuery(id+"F1.opExtrude","CAP_FACE",FACE,{"disambiguationData":[OSD([sQuery(id+"F0.wireOp",EDGE,"E0.bottom"),subQ1,subQ0,sQuery(id+"F0.wireOp",EDGE,"E1.bottom"),sQuery(id+"F0.wireOp",EDGE,"E1.top"),sQuery(id+"F0.wireOp",EDGE,"E1.left"),sQuery(id+"F0.wireOp",EDGE,"E1.right"),sQuery(id+"F0.wireOp",EDGE,"E2.bottom"),sQuery(id+"F0.wireOp",EDGE,"E2.top"),sQuery(id+"F0.wireOp",EDGE,"E2.left")])],"isStart":false})]}),makeQuery(id+"F2.opFillet","BLEND_FACE",FACE,{"disambiguationData":[OSD([subQ1,subQ0]),TDD([subQ2])]})],"blendedInto":[makeQuery(id+"F2.opFillet","BLEND_FACE",FACE,{"disambiguationData":[OSD([subQ1,subQ0]),TDD([subQ2])]})]});}
            var Q30;
            {var subQ0=sQuery(id+"F0.wireOp",EDGE,"E0.top");var subQ1=sQuery(id+"F0.wireOp",EDGE,"E0.left");Q30=makeQuery(id+"F3.opFillet","BLEND_EDGE",EDGE,{"blendedFrom":[makeQuery(id+"F2.opFillet","BLEND_EDGE",EDGE,{"blendedFrom":[makeQuery(id+"F1.opExtrude","SWEPT_EDGE",EDGE,{"disambiguationData":[OSD([subQ0,subQ1])]}),makeQuery(id+"F1.opExtrude","CAP_FACE",FACE,{"disambiguationData":[OSD([sQuery(id+"F0.wireOp",EDGE,"E0.bottom"),subQ0,subQ1,sQuery(id+"F0.wireOp",EDGE,"E1.bottom"),sQuery(id+"F0.wireOp",EDGE,"E1.top"),sQuery(id+"F0.wireOp",EDGE,"E1.left"),sQuery(id+"F0.wireOp",EDGE,"E1.right"),sQuery(id+"F0.wireOp",EDGE,"E2.bottom"),sQuery(id+"F0.wireOp",EDGE,"E2.top"),sQuery(id+"F0.wireOp",EDGE,"E2.left")])],"isStart":false})],"blendedInto":[makeQuery(id+"F1.opExtrude","CAP_FACE",FACE,{"disambiguationData":[OSD([sQuery(id+"F0.wireOp",EDGE,"E0.bottom"),subQ0,subQ1,sQuery(id+"F0.wireOp",EDGE,"E1.bottom"),sQuery(id+"F0.wireOp",EDGE,"E1.top"),sQuery(id+"F0.wireOp",EDGE,"E1.left"),sQuery(id+"F0.wireOp",EDGE,"E1.right"),sQuery(id+"F0.wireOp",EDGE,"E2.bottom"),sQuery(id+"F0.wireOp",EDGE,"E2.top"),sQuery(id+"F0.wireOp",EDGE,"E2.left")])],"isStart":false})]}),makeQuery(id+"F1.opExtrude","CAP_EDGE",EDGE,{"disambiguationData":[OSD([subQ0])],"isStart":false})],"blendedInto":[]});}
            var Q31;
            {var subQ0=sQuery(id+"F0.wireOp",EDGE,"E2.top");var subQ1=sQuery(id+"F0.wireOp",EDGE,"E1.top");var subQ2=sQuery(id+"F0.wireOp",EDGE,"E2.left");Q31=makeQuery(id+"F3.opFillet","BLEND_EDGE",EDGE,{"blendedFrom":[makeQuery(id+"F2.opFillet","BLEND_EDGE",EDGE,{"blendedFrom":[makeQuery(id+"F1.opExtrude","SWEPT_EDGE",EDGE,{"disambiguationData":[OSD([subQ0,subQ2])]}),makeQuery(id+"F1.opExtrude","CAP_FACE",FACE,{"disambiguationData":[OSD([sQuery(id+"F0.wireOp",EDGE,"E0.bottom"),sQuery(id+"F0.wireOp",EDGE,"E0.top"),sQuery(id+"F0.wireOp",EDGE,"E0.left"),sQuery(id+"F0.wireOp",EDGE,"E1.bottom"),subQ1,sQuery(id+"F0.wireOp",EDGE,"E1.left"),sQuery(id+"F0.wireOp",EDGE,"E1.right"),sQuery(id+"F0.wireOp",EDGE,"E2.bottom"),subQ0,subQ2])],"isStart":false})],"blendedInto":[makeQuery(id+"F1.opExtrude","CAP_FACE",FACE,{"disambiguationData":[OSD([sQuery(id+"F0.wireOp",EDGE,"E0.bottom"),sQuery(id+"F0.wireOp",EDGE,"E0.top"),sQuery(id+"F0.wireOp",EDGE,"E0.left"),sQuery(id+"F0.wireOp",EDGE,"E1.bottom"),subQ1,sQuery(id+"F0.wireOp",EDGE,"E1.left"),sQuery(id+"F0.wireOp",EDGE,"E1.right"),sQuery(id+"F0.wireOp",EDGE,"E2.bottom"),subQ0,subQ2])],"isStart":false})]}),makeQuery(id+"F1.opExtrude","CAP_EDGE",EDGE,{"disambiguationData":[OSD([subQ1,subQ0])],"isStart":false})],"blendedInto":[]});}
            var Q32;
            {var subQ0=sQuery(id+"F0.wireOp",EDGE,"E0.left");var subQ1=sQuery(id+"F0.wireOp",EDGE,"E0.top");Q32=makeQuery(id+"F3.opFillet","BLEND_EDGE",EDGE,{"blendedFrom":[makeQuery(id+"F2.opFillet","BLEND_EDGE",EDGE,{"blendedFrom":[makeQuery(id+"F1.opExtrude","SWEPT_EDGE",EDGE,{"disambiguationData":[OSD([subQ1,subQ0])]}),makeQuery(id+"F1.opExtrude","CAP_FACE",FACE,{"disambiguationData":[OSD([sQuery(id+"F0.wireOp",EDGE,"E0.bottom"),subQ1,subQ0,sQuery(id+"F0.wireOp",EDGE,"E1.bottom"),sQuery(id+"F0.wireOp",EDGE,"E1.top"),sQuery(id+"F0.wireOp",EDGE,"E1.left"),sQuery(id+"F0.wireOp",EDGE,"E1.right"),sQuery(id+"F0.wireOp",EDGE,"E2.bottom"),sQuery(id+"F0.wireOp",EDGE,"E2.top"),sQuery(id+"F0.wireOp",EDGE,"E2.left")])],"isStart":false})],"blendedInto":[makeQuery(id+"F1.opExtrude","CAP_FACE",FACE,{"disambiguationData":[OSD([sQuery(id+"F0.wireOp",EDGE,"E0.bottom"),subQ1,subQ0,sQuery(id+"F0.wireOp",EDGE,"E1.bottom"),sQuery(id+"F0.wireOp",EDGE,"E1.top"),sQuery(id+"F0.wireOp",EDGE,"E1.left"),sQuery(id+"F0.wireOp",EDGE,"E1.right"),sQuery(id+"F0.wireOp",EDGE,"E2.bottom"),sQuery(id+"F0.wireOp",EDGE,"E2.top"),sQuery(id+"F0.wireOp",EDGE,"E2.left")])],"isStart":false})]}),makeQuery(id+"F1.opExtrude","CAP_EDGE",EDGE,{"disambiguationData":[OSD([subQ0])],"isStart":false})],"blendedInto":[]});}
            var Q33;
            Q33=makeQuery(id+"F3.opFillet","BLEND_EDGE",EDGE,{"blendedFrom":[makeQuery(id+"F1.opExtrude","CAP_EDGE",EDGE,{"disambiguationData":[OSD([sQuery(id+"F0.wireOp",EDGE,"E0.bottom"),sQuery(id+"F0.wireOp",EDGE,"E1.bottom")])],"isStart":false}),makeQuery(id+"F1.opExtrude","CAP_EDGE",EDGE,{"disambiguationData":[OSD([sQuery(id+"F0.wireOp",EDGE,"E0.left")])],"isStart":false})],"blendedInto":[]});
            var Q34;
            {var subQ0=sQuery(id+"F0.wireOp",EDGE,"E0.top");Q34=makeQuery(id+"F3.opFillet","BLEND_EDGE",EDGE,{"blendedFrom":[makeQuery(id+"F1.opExtrude","CAP_EDGE",EDGE,{"disambiguationData":[OSD([subQ0])],"isStart":false}),makeQuery(id+"F1.opExtrude","CAP_FACE",FACE,{"disambiguationData":[OSD([sQuery(id+"F0.wireOp",EDGE,"E0.bottom"),subQ0,sQuery(id+"F0.wireOp",EDGE,"E0.left"),sQuery(id+"F0.wireOp",EDGE,"E1.bottom"),sQuery(id+"F0.wireOp",EDGE,"E1.top"),sQuery(id+"F0.wireOp",EDGE,"E1.left"),sQuery(id+"F0.wireOp",EDGE,"E1.right"),sQuery(id+"F0.wireOp",EDGE,"E2.bottom"),sQuery(id+"F0.wireOp",EDGE,"E2.top"),sQuery(id+"F0.wireOp",EDGE,"E2.left")])],"isStart":false})],"blendedInto":[makeQuery(id+"F1.opExtrude","CAP_FACE",FACE,{"disambiguationData":[OSD([sQuery(id+"F0.wireOp",EDGE,"E0.bottom"),subQ0,sQuery(id+"F0.wireOp",EDGE,"E0.left"),sQuery(id+"F0.wireOp",EDGE,"E1.bottom"),sQuery(id+"F0.wireOp",EDGE,"E1.top"),sQuery(id+"F0.wireOp",EDGE,"E1.left"),sQuery(id+"F0.wireOp",EDGE,"E1.right"),sQuery(id+"F0.wireOp",EDGE,"E2.bottom"),sQuery(id+"F0.wireOp",EDGE,"E2.top"),sQuery(id+"F0.wireOp",EDGE,"E2.left")])],"isStart":false})]});}
            var Q35;
            {var subQ0=sQuery(id+"F0.wireOp",EDGE,"E0.top");Q35=makeQuery(id+"F3.opFillet","BLEND_EDGE",EDGE,{"blendedFrom":[makeQuery(id+"F1.opExtrude","CAP_EDGE",EDGE,{"disambiguationData":[OSD([subQ0])],"isStart":false}),makeQuery(id+"F1.opExtrude","SWEPT_FACE",FACE,{"disambiguationData":[OSD([subQ0])]})],"blendedInto":[makeQuery(id+"F1.opExtrude","SWEPT_FACE",FACE,{"disambiguationData":[OSD([subQ0])]})]});}
            var Q36;
            {var subQ0=sQuery(id+"F0.wireOp",EDGE,"E1.bottom");var subQ1=sQuery(id+"F0.wireOp",EDGE,"E0.bottom");Q36=makeQuery(id+"F3.opFillet","BLEND_EDGE",EDGE,{"blendedFrom":[makeQuery(id+"F1.opExtrude","CAP_EDGE",EDGE,{"disambiguationData":[OSD([subQ1,subQ0])],"isStart":false}),makeQuery(id+"F1.opExtrude","CAP_FACE",FACE,{"disambiguationData":[OSD([subQ1,sQuery(id+"F0.wireOp",EDGE,"E0.top"),sQuery(id+"F0.wireOp",EDGE,"E0.left"),subQ0,sQuery(id+"F0.wireOp",EDGE,"E1.top"),sQuery(id+"F0.wireOp",EDGE,"E1.left"),sQuery(id+"F0.wireOp",EDGE,"E1.right"),sQuery(id+"F0.wireOp",EDGE,"E2.bottom"),sQuery(id+"F0.wireOp",EDGE,"E2.top"),sQuery(id+"F0.wireOp",EDGE,"E2.left")])],"isStart":false})],"blendedInto":[makeQuery(id+"F1.opExtrude","CAP_FACE",FACE,{"disambiguationData":[OSD([subQ1,sQuery(id+"F0.wireOp",EDGE,"E0.top"),sQuery(id+"F0.wireOp",EDGE,"E0.left"),subQ0,sQuery(id+"F0.wireOp",EDGE,"E1.top"),sQuery(id+"F0.wireOp",EDGE,"E1.left"),sQuery(id+"F0.wireOp",EDGE,"E1.right"),sQuery(id+"F0.wireOp",EDGE,"E2.bottom"),sQuery(id+"F0.wireOp",EDGE,"E2.top"),sQuery(id+"F0.wireOp",EDGE,"E2.left")])],"isStart":false})]});}
            var Q37;
            {var subQ0=sQuery(id+"F0.wireOp",EDGE,"E0.left");Q37=makeQuery(id+"F3.opFillet","BLEND_EDGE",EDGE,{"blendedFrom":[makeQuery(id+"F1.opExtrude","CAP_EDGE",EDGE,{"disambiguationData":[OSD([subQ0])],"isStart":false}),makeQuery(id+"F1.opExtrude","CAP_FACE",FACE,{"disambiguationData":[OSD([sQuery(id+"F0.wireOp",EDGE,"E0.bottom"),sQuery(id+"F0.wireOp",EDGE,"E0.top"),subQ0,sQuery(id+"F0.wireOp",EDGE,"E1.bottom"),sQuery(id+"F0.wireOp",EDGE,"E1.top"),sQuery(id+"F0.wireOp",EDGE,"E1.left"),sQuery(id+"F0.wireOp",EDGE,"E1.right"),sQuery(id+"F0.wireOp",EDGE,"E2.bottom"),sQuery(id+"F0.wireOp",EDGE,"E2.top"),sQuery(id+"F0.wireOp",EDGE,"E2.left")])],"isStart":false})],"blendedInto":[makeQuery(id+"F1.opExtrude","CAP_FACE",FACE,{"disambiguationData":[OSD([sQuery(id+"F0.wireOp",EDGE,"E0.bottom"),sQuery(id+"F0.wireOp",EDGE,"E0.top"),subQ0,sQuery(id+"F0.wireOp",EDGE,"E1.bottom"),sQuery(id+"F0.wireOp",EDGE,"E1.top"),sQuery(id+"F0.wireOp",EDGE,"E1.left"),sQuery(id+"F0.wireOp",EDGE,"E1.right"),sQuery(id+"F0.wireOp",EDGE,"E2.bottom"),sQuery(id+"F0.wireOp",EDGE,"E2.top"),sQuery(id+"F0.wireOp",EDGE,"E2.left")])],"isStart":false})]});}
            var Q38;
            {var subQ0=sQuery(id+"F0.wireOp",EDGE,"E0.left");Q38=makeQuery(id+"F3.opFillet","BLEND_EDGE",EDGE,{"blendedFrom":[makeQuery(id+"F1.opExtrude","CAP_EDGE",EDGE,{"disambiguationData":[OSD([subQ0])],"isStart":false}),makeQuery(id+"F1.opExtrude","SWEPT_FACE",FACE,{"disambiguationData":[OSD([subQ0])]})],"blendedInto":[makeQuery(id+"F1.opExtrude","SWEPT_FACE",FACE,{"disambiguationData":[OSD([subQ0])]})]});}
            var Q39;
            {var subQ0=sQuery(id+"F0.wireOp",EDGE,"E2.left");Q39=makeQuery(id+"F3.opFillet","BLEND_EDGE",EDGE,{"blendedFrom":[makeQuery(id+"F1.opExtrude","CAP_EDGE",EDGE,{"disambiguationData":[OSD([subQ0])],"isStart":false}),makeQuery(id+"F1.opExtrude","CAP_FACE",FACE,{"disambiguationData":[OSD([sQuery(id+"F0.wireOp",EDGE,"E0.bottom"),sQuery(id+"F0.wireOp",EDGE,"E0.top"),sQuery(id+"F0.wireOp",EDGE,"E0.left"),sQuery(id+"F0.wireOp",EDGE,"E1.bottom"),sQuery(id+"F0.wireOp",EDGE,"E1.top"),sQuery(id+"F0.wireOp",EDGE,"E1.left"),sQuery(id+"F0.wireOp",EDGE,"E1.right"),sQuery(id+"F0.wireOp",EDGE,"E2.bottom"),sQuery(id+"F0.wireOp",EDGE,"E2.top"),subQ0])],"isStart":false})],"blendedInto":[makeQuery(id+"F1.opExtrude","CAP_FACE",FACE,{"disambiguationData":[OSD([sQuery(id+"F0.wireOp",EDGE,"E0.bottom"),sQuery(id+"F0.wireOp",EDGE,"E0.top"),sQuery(id+"F0.wireOp",EDGE,"E0.left"),sQuery(id+"F0.wireOp",EDGE,"E1.bottom"),sQuery(id+"F0.wireOp",EDGE,"E1.top"),sQuery(id+"F0.wireOp",EDGE,"E1.left"),sQuery(id+"F0.wireOp",EDGE,"E1.right"),sQuery(id+"F0.wireOp",EDGE,"E2.bottom"),sQuery(id+"F0.wireOp",EDGE,"E2.top"),subQ0])],"isStart":false})]});}
            var Q40;
            {var subQ0=sQuery(id+"F0.wireOp",EDGE,"E2.left");var subQ1=sQuery(id+"F0.wireOp",EDGE,"E2.top");Q40=makeQuery(id+"F3.opFillet","BLEND_EDGE",EDGE,{"blendedFrom":[makeQuery(id+"F2.opFillet","BLEND_EDGE",EDGE,{"blendedFrom":[makeQuery(id+"F1.opExtrude","SWEPT_EDGE",EDGE,{"disambiguationData":[OSD([subQ1,subQ0])]}),makeQuery(id+"F1.opExtrude","CAP_FACE",FACE,{"disambiguationData":[OSD([sQuery(id+"F0.wireOp",EDGE,"E0.bottom"),sQuery(id+"F0.wireOp",EDGE,"E0.top"),sQuery(id+"F0.wireOp",EDGE,"E0.left"),sQuery(id+"F0.wireOp",EDGE,"E1.bottom"),sQuery(id+"F0.wireOp",EDGE,"E1.top"),sQuery(id+"F0.wireOp",EDGE,"E1.left"),sQuery(id+"F0.wireOp",EDGE,"E1.right"),sQuery(id+"F0.wireOp",EDGE,"E2.bottom"),subQ1,subQ0])],"isStart":false})],"blendedInto":[makeQuery(id+"F1.opExtrude","CAP_FACE",FACE,{"disambiguationData":[OSD([sQuery(id+"F0.wireOp",EDGE,"E0.bottom"),sQuery(id+"F0.wireOp",EDGE,"E0.top"),sQuery(id+"F0.wireOp",EDGE,"E0.left"),sQuery(id+"F0.wireOp",EDGE,"E1.bottom"),sQuery(id+"F0.wireOp",EDGE,"E1.top"),sQuery(id+"F0.wireOp",EDGE,"E1.left"),sQuery(id+"F0.wireOp",EDGE,"E1.right"),sQuery(id+"F0.wireOp",EDGE,"E2.bottom"),subQ1,subQ0])],"isStart":false})]}),makeQuery(id+"F1.opExtrude","CAP_EDGE",EDGE,{"disambiguationData":[OSD([subQ0])],"isStart":false})],"blendedInto":[]});}
            var Q41;
            {var subQ0=sQuery(id+"F0.wireOp",EDGE,"E2.left");var subQ1=sQuery(id+"F0.wireOp",EDGE,"E2.bottom");Q41=makeQuery(id+"F3.opFillet","BLEND_EDGE",EDGE,{"blendedFrom":[makeQuery(id+"F2.opFillet","BLEND_EDGE",EDGE,{"blendedFrom":[makeQuery(id+"F1.opExtrude","SWEPT_EDGE",EDGE,{"disambiguationData":[OSD([subQ1,subQ0])]}),makeQuery(id+"F1.opExtrude","CAP_FACE",FACE,{"disambiguationData":[OSD([sQuery(id+"F0.wireOp",EDGE,"E0.bottom"),sQuery(id+"F0.wireOp",EDGE,"E0.top"),sQuery(id+"F0.wireOp",EDGE,"E0.left"),sQuery(id+"F0.wireOp",EDGE,"E1.bottom"),sQuery(id+"F0.wireOp",EDGE,"E1.top"),sQuery(id+"F0.wireOp",EDGE,"E1.left"),sQuery(id+"F0.wireOp",EDGE,"E1.right"),subQ1,sQuery(id+"F0.wireOp",EDGE,"E2.top"),subQ0])],"isStart":false})],"blendedInto":[makeQuery(id+"F1.opExtrude","CAP_FACE",FACE,{"disambiguationData":[OSD([sQuery(id+"F0.wireOp",EDGE,"E0.bottom"),sQuery(id+"F0.wireOp",EDGE,"E0.top"),sQuery(id+"F0.wireOp",EDGE,"E0.left"),sQuery(id+"F0.wireOp",EDGE,"E1.bottom"),sQuery(id+"F0.wireOp",EDGE,"E1.top"),sQuery(id+"F0.wireOp",EDGE,"E1.left"),sQuery(id+"F0.wireOp",EDGE,"E1.right"),subQ1,sQuery(id+"F0.wireOp",EDGE,"E2.top"),subQ0])],"isStart":false})]}),makeQuery(id+"F1.opExtrude","CAP_EDGE",EDGE,{"disambiguationData":[OSD([subQ0])],"isStart":false})],"blendedInto":[]});}
            var Q42;
            {var subQ0=sQuery(id+"F0.wireOp",EDGE,"E1.right");Q42=makeQuery(id+"F3.opFillet","BLEND_EDGE",EDGE,{"blendedFrom":[makeQuery(id+"F1.opExtrude","CAP_EDGE",EDGE,{"disambiguationData":[OSD([sQuery(id+"F0.wireOp",EDGE,"E0.bottom"),sQuery(id+"F0.wireOp",EDGE,"E1.bottom")])],"isStart":false}),makeQuery(id+"F2.opFillet","BLEND_FACE",FACE,{"disambiguationData":[OSD([subQ0]),TDD([makeQuery(id+"F1.opExtrude","CAP_EDGE",EDGE,{"disambiguationData":[OSD([subQ0])],"isStart":false})])]})],"blendedInto":[makeQuery(id+"F2.opFillet","BLEND_FACE",FACE,{"disambiguationData":[OSD([subQ0]),TDD([makeQuery(id+"F1.opExtrude","CAP_EDGE",EDGE,{"disambiguationData":[OSD([subQ0])],"isStart":false})])]})]});}
            var Q43;
            {var subQ0=sQuery(id+"F0.wireOp",EDGE,"E1.bottom");var subQ1=sQuery(id+"F0.wireOp",EDGE,"E0.bottom");Q43=makeQuery(id+"F3.opFillet","BLEND_EDGE",EDGE,{"blendedFrom":[makeQuery(id+"F1.opExtrude","CAP_EDGE",EDGE,{"disambiguationData":[OSD([subQ1,subQ0])],"isStart":false}),makeQuery(id+"F1.opExtrude","SWEPT_FACE",FACE,{"disambiguationData":[OSD([subQ1,subQ0])]})],"blendedInto":[makeQuery(id+"F1.opExtrude","SWEPT_FACE",FACE,{"disambiguationData":[OSD([subQ1,subQ0])]})]});}
            var Q44;
            {var subQ0=sQuery(id+"F0.wireOp",EDGE,"E2.left");Q44=makeQuery(id+"F3.opFillet","BLEND_EDGE",EDGE,{"blendedFrom":[makeQuery(id+"F1.opExtrude","CAP_EDGE",EDGE,{"disambiguationData":[OSD([subQ0])],"isStart":false}),makeQuery(id+"F1.opExtrude","SWEPT_FACE",FACE,{"disambiguationData":[OSD([subQ0])]})],"blendedInto":[makeQuery(id+"F1.opExtrude","SWEPT_FACE",FACE,{"disambiguationData":[OSD([subQ0])]})]});}
            var Q45;
            {var subQ0=sQuery(id+"F0.wireOp",EDGE,"E0.left");var subQ1=sQuery(id+"F0.wireOp",EDGE,"E0.top");Q45=makeQuery(id+"F2.opFillet","BLEND_EDGE",EDGE,{"blendedFrom":[makeQuery(id+"F1.opExtrude","CAP_VERTEX",VERTEX,{"disambiguationData":[OSD([subQ1,subQ0])],"isStart":true}),makeQuery(id+"F1.opExtrude","SWEPT_EDGE",EDGE,{"disambiguationData":[OSD([subQ1,subQ0])]})],"blendedInto":[]});}
            var Q46;
            Q46=makeQuery(id+"F1.opExtrude","SWEPT_EDGE",EDGE,{"disambiguationData":[OSD([sQuery(id+"F0.wireOp",EDGE,"E0.top"),sQuery(id+"F0.wireOp",EDGE,"E1.left")])]});
            var Q47;
            {var subQ0=sQuery(id+"F0.wireOp",EDGE,"E0.left");Q47=makeQuery(id+"F2.opFillet","BLEND_EDGE",EDGE,{"blendedFrom":[makeQuery(id+"F1.opExtrude","CAP_VERTEX",VERTEX,{"disambiguationData":[OSD([sQuery(id+"F0.wireOp",EDGE,"E0.top"),subQ0])],"isStart":true}),makeQuery(id+"F1.opExtrude","CAP_EDGE",EDGE,{"disambiguationData":[OSD([subQ0])],"isStart":true})],"blendedInto":[]});}
            var Q48;
            Q48=makeQuery(id+"F2.opFillet","BLEND_EDGE",EDGE,{"blendedFrom":[makeQuery(id+"F1.opExtrude","CAP_EDGE",EDGE,{"disambiguationData":[OSD([sQuery(id+"F0.wireOp",EDGE,"E0.top")])],"isStart":true}),makeQuery(id+"F1.opExtrude","CAP_EDGE",EDGE,{"disambiguationData":[OSD([sQuery(id+"F0.wireOp",EDGE,"E1.left")])],"isStart":true})],"blendedInto":[]});
            var Q49;
            {var subQ0=sQuery(id+"F0.wireOp",EDGE,"E0.top");Q49=makeQuery(id+"F2.opFillet","BLEND_EDGE",EDGE,{"blendedFrom":[makeQuery(id+"F1.opExtrude","SWEPT_EDGE",EDGE,{"disambiguationData":[OSD([subQ0,sQuery(id+"F0.wireOp",EDGE,"E0.left")])]}),makeQuery(id+"F1.opExtrude","SWEPT_FACE",FACE,{"disambiguationData":[OSD([subQ0])]})],"blendedInto":[makeQuery(id+"F1.opExtrude","SWEPT_FACE",FACE,{"disambiguationData":[OSD([subQ0])]})]});}
            var Q50;
            {var subQ0=sQuery(id+"F0.wireOp",EDGE,"E0.top");Q50=makeQuery(id+"F2.opFillet","BLEND_EDGE",EDGE,{"blendedFrom":[makeQuery(id+"F1.opExtrude","CAP_EDGE",EDGE,{"disambiguationData":[OSD([subQ0])],"isStart":true}),makeQuery(id+"F1.opExtrude","CAP_FACE",FACE,{"disambiguationData":[OSD([sQuery(id+"F0.wireOp",EDGE,"E0.bottom"),subQ0,sQuery(id+"F0.wireOp",EDGE,"E0.left"),sQuery(id+"F0.wireOp",EDGE,"E1.bottom"),sQuery(id+"F0.wireOp",EDGE,"E1.top"),sQuery(id+"F0.wireOp",EDGE,"E1.left"),sQuery(id+"F0.wireOp",EDGE,"E1.right"),sQuery(id+"F0.wireOp",EDGE,"E2.bottom"),sQuery(id+"F0.wireOp",EDGE,"E2.top"),sQuery(id+"F0.wireOp",EDGE,"E2.left")])],"isStart":true})],"blendedInto":[makeQuery(id+"F1.opExtrude","CAP_FACE",FACE,{"disambiguationData":[OSD([sQuery(id+"F0.wireOp",EDGE,"E0.bottom"),subQ0,sQuery(id+"F0.wireOp",EDGE,"E0.left"),sQuery(id+"F0.wireOp",EDGE,"E1.bottom"),sQuery(id+"F0.wireOp",EDGE,"E1.top"),sQuery(id+"F0.wireOp",EDGE,"E1.left"),sQuery(id+"F0.wireOp",EDGE,"E1.right"),sQuery(id+"F0.wireOp",EDGE,"E2.bottom"),sQuery(id+"F0.wireOp",EDGE,"E2.top"),sQuery(id+"F0.wireOp",EDGE,"E2.left")])],"isStart":true})]});}
            var Q51;
            {var subQ0=sQuery(id+"F0.wireOp",EDGE,"E0.top");Q51=makeQuery(id+"F2.opFillet","BLEND_EDGE",EDGE,{"blendedFrom":[makeQuery(id+"F1.opExtrude","CAP_EDGE",EDGE,{"disambiguationData":[OSD([subQ0])],"isStart":true}),makeQuery(id+"F1.opExtrude","SWEPT_FACE",FACE,{"disambiguationData":[OSD([subQ0])]})],"blendedInto":[makeQuery(id+"F1.opExtrude","SWEPT_FACE",FACE,{"disambiguationData":[OSD([subQ0])]})]});}
            var Q52;
            {var subQ0=sQuery(id+"F0.wireOp",EDGE,"E0.left");Q52=makeQuery(id+"F2.opFillet","BLEND_EDGE",EDGE,{"blendedFrom":[makeQuery(id+"F1.opExtrude","CAP_EDGE",EDGE,{"disambiguationData":[OSD([subQ0])],"isStart":true}),makeQuery(id+"F1.opExtrude","CAP_FACE",FACE,{"disambiguationData":[OSD([sQuery(id+"F0.wireOp",EDGE,"E0.bottom"),sQuery(id+"F0.wireOp",EDGE,"E0.top"),subQ0,sQuery(id+"F0.wireOp",EDGE,"E1.bottom"),sQuery(id+"F0.wireOp",EDGE,"E1.top"),sQuery(id+"F0.wireOp",EDGE,"E1.left"),sQuery(id+"F0.wireOp",EDGE,"E1.right"),sQuery(id+"F0.wireOp",EDGE,"E2.bottom"),sQuery(id+"F0.wireOp",EDGE,"E2.top"),sQuery(id+"F0.wireOp",EDGE,"E2.left")])],"isStart":true})],"blendedInto":[makeQuery(id+"F1.opExtrude","CAP_FACE",FACE,{"disambiguationData":[OSD([sQuery(id+"F0.wireOp",EDGE,"E0.bottom"),sQuery(id+"F0.wireOp",EDGE,"E0.top"),subQ0,sQuery(id+"F0.wireOp",EDGE,"E1.bottom"),sQuery(id+"F0.wireOp",EDGE,"E1.top"),sQuery(id+"F0.wireOp",EDGE,"E1.left"),sQuery(id+"F0.wireOp",EDGE,"E1.right"),sQuery(id+"F0.wireOp",EDGE,"E2.bottom"),sQuery(id+"F0.wireOp",EDGE,"E2.top"),sQuery(id+"F0.wireOp",EDGE,"E2.left")])],"isStart":true})]});}
            var Q53;
            {var subQ0=sQuery(id+"F0.wireOp",EDGE,"E0.left");Q53=makeQuery(id+"F2.opFillet","BLEND_EDGE",EDGE,{"blendedFrom":[makeQuery(id+"F1.opExtrude","CAP_EDGE",EDGE,{"disambiguationData":[OSD([subQ0])],"isStart":true}),makeQuery(id+"F1.opExtrude","SWEPT_FACE",FACE,{"disambiguationData":[OSD([subQ0])]})],"blendedInto":[makeQuery(id+"F1.opExtrude","SWEPT_FACE",FACE,{"disambiguationData":[OSD([subQ0])]})]});}
            var Q54;
            {var subQ0=sQuery(id+"F0.wireOp",EDGE,"E2.top");Q54=makeQuery(id+"F2.opFillet","BLEND_EDGE",EDGE,{"blendedFrom":[makeQuery(id+"F1.opExtrude","SWEPT_EDGE",EDGE,{"disambiguationData":[OSD([subQ0,sQuery(id+"F0.wireOp",EDGE,"E2.left")])]}),makeQuery(id+"F1.opExtrude","SWEPT_FACE",FACE,{"disambiguationData":[OSD([sQuery(id+"F0.wireOp",EDGE,"E1.top"),subQ0])]})],"blendedInto":[makeQuery(id+"F1.opExtrude","SWEPT_FACE",FACE,{"disambiguationData":[OSD([sQuery(id+"F0.wireOp",EDGE,"E1.top"),subQ0])]})]});}
            var Q55;
            {var subQ0=sQuery(id+"F0.wireOp",EDGE,"E1.right");var subQ1=sQuery(id+"F0.wireOp",EDGE,"E1.bottom");Q55=makeQuery(id+"F3.opFillet","BLEND_EDGE",EDGE,{"blendedFrom":[makeQuery(id+"F1.opExtrude","CAP_EDGE",EDGE,{"disambiguationData":[OSD([sQuery(id+"F0.wireOp",EDGE,"E0.bottom"),subQ1])],"isStart":false}),makeQuery(id+"F2.opFillet","BLEND_FACE",FACE,{"disambiguationData":[OSD([subQ1,subQ0]),TDD([makeQuery(id+"F1.opExtrude","SWEPT_EDGE",EDGE,{"disambiguationData":[OSD([subQ1,subQ0])]})])]})],"blendedInto":[makeQuery(id+"F2.opFillet","BLEND_FACE",FACE,{"disambiguationData":[OSD([subQ1,subQ0]),TDD([makeQuery(id+"F1.opExtrude","SWEPT_EDGE",EDGE,{"disambiguationData":[OSD([subQ1,subQ0])]})])]})]});}
            var Q56;
            {var subQ0=sQuery(id+"F0.wireOp",EDGE,"E0.left");Q56=makeQuery(id+"F2.opFillet","BLEND_EDGE",EDGE,{"blendedFrom":[makeQuery(id+"F1.opExtrude","SWEPT_EDGE",EDGE,{"disambiguationData":[OSD([sQuery(id+"F0.wireOp",EDGE,"E0.top"),subQ0])]}),makeQuery(id+"F1.opExtrude","SWEPT_FACE",FACE,{"disambiguationData":[OSD([subQ0])]})],"blendedInto":[makeQuery(id+"F1.opExtrude","SWEPT_FACE",FACE,{"disambiguationData":[OSD([subQ0])]})]});}
            var Q57;
            {var subQ0=sQuery(id+"F0.wireOp",EDGE,"E2.bottom");Q57=makeQuery(id+"F2.opFillet","BLEND_EDGE",EDGE,{"blendedFrom":[makeQuery(id+"F1.opExtrude","SWEPT_EDGE",EDGE,{"disambiguationData":[OSD([subQ0,sQuery(id+"F0.wireOp",EDGE,"E2.left")])]}),makeQuery(id+"F1.opExtrude","SWEPT_FACE",FACE,{"disambiguationData":[OSD([subQ0])]})],"blendedInto":[makeQuery(id+"F1.opExtrude","SWEPT_FACE",FACE,{"disambiguationData":[OSD([subQ0])]})]});}
            var Q58;
            Q58=makeQuery(id+"F1.opExtrude","SWEPT_EDGE",EDGE,{"disambiguationData":[OSD([sQuery(id+"F0.wireOp",EDGE,"E0.bottom"),sQuery(id+"F0.wireOp",EDGE,"E0.left")])]});
            var Q59;
            {var subQ0=sQuery(id+"F0.wireOp",EDGE,"E2.left");var subQ1=sQuery(id+"F0.wireOp",EDGE,"E2.bottom");var subQ2=makeQuery(id+"F1.opExtrude","SWEPT_EDGE",EDGE,{"disambiguationData":[OSD([subQ1,subQ0])]});Q59=makeQuery(id+"F3.opFillet","BLEND_EDGE",EDGE,{"blendedFrom":[makeQuery(id+"F2.opFillet","BLEND_EDGE",EDGE,{"blendedFrom":[subQ2,makeQuery(id+"F1.opExtrude","CAP_FACE",FACE,{"disambiguationData":[OSD([sQuery(id+"F0.wireOp",EDGE,"E0.bottom"),sQuery(id+"F0.wireOp",EDGE,"E0.top"),sQuery(id+"F0.wireOp",EDGE,"E0.left"),sQuery(id+"F0.wireOp",EDGE,"E1.bottom"),sQuery(id+"F0.wireOp",EDGE,"E1.top"),sQuery(id+"F0.wireOp",EDGE,"E1.left"),sQuery(id+"F0.wireOp",EDGE,"E1.right"),subQ1,sQuery(id+"F0.wireOp",EDGE,"E2.top"),subQ0])],"isStart":false})],"blendedInto":[makeQuery(id+"F1.opExtrude","CAP_FACE",FACE,{"disambiguationData":[OSD([sQuery(id+"F0.wireOp",EDGE,"E0.bottom"),sQuery(id+"F0.wireOp",EDGE,"E0.top"),sQuery(id+"F0.wireOp",EDGE,"E0.left"),sQuery(id+"F0.wireOp",EDGE,"E1.bottom"),sQuery(id+"F0.wireOp",EDGE,"E1.top"),sQuery(id+"F0.wireOp",EDGE,"E1.left"),sQuery(id+"F0.wireOp",EDGE,"E1.right"),subQ1,sQuery(id+"F0.wireOp",EDGE,"E2.top"),subQ0])],"isStart":false})]}),makeQuery(id+"F2.opFillet","BLEND_FACE",FACE,{"disambiguationData":[OSD([subQ1,subQ0]),TDD([subQ2])]})],"blendedInto":[makeQuery(id+"F2.opFillet","BLEND_FACE",FACE,{"disambiguationData":[OSD([subQ1,subQ0]),TDD([subQ2])]})]});}
            var Q60;
            {var subQ0=sQuery(id+"F0.wireOp",EDGE,"E0.top");Q60=makeQuery(id+"F2.opFillet","BLEND_EDGE",EDGE,{"blendedFrom":[makeQuery(id+"F1.opExtrude","CAP_VERTEX",VERTEX,{"disambiguationData":[OSD([subQ0,sQuery(id+"F0.wireOp",EDGE,"E0.left")])],"isStart":true}),makeQuery(id+"F1.opExtrude","CAP_EDGE",EDGE,{"disambiguationData":[OSD([subQ0])],"isStart":true})],"blendedInto":[]});}
            var Q61;
            {var subQ0=sQuery(id+"F0.wireOp",EDGE,"E2.left");Q61=makeQuery(id+"F2.opFillet","BLEND_EDGE",EDGE,{"blendedFrom":[makeQuery(id+"F1.opExtrude","SWEPT_EDGE",EDGE,{"disambiguationData":[OSD([sQuery(id+"F0.wireOp",EDGE,"E2.bottom"),subQ0])]}),makeQuery(id+"F1.opExtrude","SWEPT_FACE",FACE,{"disambiguationData":[OSD([subQ0])]})],"blendedInto":[makeQuery(id+"F1.opExtrude","SWEPT_FACE",FACE,{"disambiguationData":[OSD([subQ0])]})]});}
            var Q62;
            {var subQ0=sQuery(id+"F0.wireOp",EDGE,"E2.left");var subQ1=sQuery(id+"F0.wireOp",EDGE,"E2.top");var subQ2=makeQuery(id+"F1.opExtrude","SWEPT_EDGE",EDGE,{"disambiguationData":[OSD([subQ1,subQ0])]});Q62=makeQuery(id+"F3.opFillet","BLEND_EDGE",EDGE,{"blendedFrom":[makeQuery(id+"F2.opFillet","BLEND_EDGE",EDGE,{"blendedFrom":[subQ2,makeQuery(id+"F1.opExtrude","CAP_FACE",FACE,{"disambiguationData":[OSD([sQuery(id+"F0.wireOp",EDGE,"E0.bottom"),sQuery(id+"F0.wireOp",EDGE,"E0.top"),sQuery(id+"F0.wireOp",EDGE,"E0.left"),sQuery(id+"F0.wireOp",EDGE,"E1.bottom"),sQuery(id+"F0.wireOp",EDGE,"E1.top"),sQuery(id+"F0.wireOp",EDGE,"E1.left"),sQuery(id+"F0.wireOp",EDGE,"E1.right"),sQuery(id+"F0.wireOp",EDGE,"E2.bottom"),subQ1,subQ0])],"isStart":false})],"blendedInto":[makeQuery(id+"F1.opExtrude","CAP_FACE",FACE,{"disambiguationData":[OSD([sQuery(id+"F0.wireOp",EDGE,"E0.bottom"),sQuery(id+"F0.wireOp",EDGE,"E0.top"),sQuery(id+"F0.wireOp",EDGE,"E0.left"),sQuery(id+"F0.wireOp",EDGE,"E1.bottom"),sQuery(id+"F0.wireOp",EDGE,"E1.top"),sQuery(id+"F0.wireOp",EDGE,"E1.left"),sQuery(id+"F0.wireOp",EDGE,"E1.right"),sQuery(id+"F0.wireOp",EDGE,"E2.bottom"),subQ1,subQ0])],"isStart":false})]}),makeQuery(id+"F2.opFillet","BLEND_FACE",FACE,{"disambiguationData":[OSD([subQ1,subQ0]),TDD([subQ2])]})],"blendedInto":[makeQuery(id+"F2.opFillet","BLEND_FACE",FACE,{"disambiguationData":[OSD([subQ1,subQ0]),TDD([subQ2])]})]});}
            var Q63;
            {var subQ0=sQuery(id+"F0.wireOp",EDGE,"E1.bottom");var subQ1=sQuery(id+"F0.wireOp",EDGE,"E0.bottom");Q63=makeQuery(id+"F2.opFillet","BLEND_EDGE",EDGE,{"blendedFrom":[makeQuery(id+"F1.opExtrude","CAP_EDGE",EDGE,{"disambiguationData":[OSD([subQ1,subQ0])],"isStart":true}),makeQuery(id+"F1.opExtrude","SWEPT_FACE",FACE,{"disambiguationData":[OSD([subQ1,subQ0])]})],"blendedInto":[makeQuery(id+"F1.opExtrude","SWEPT_FACE",FACE,{"disambiguationData":[OSD([subQ1,subQ0])]})]});}
            var Q64;
            {var subQ0=sQuery(id+"F0.wireOp",EDGE,"E1.right");Q64=makeQuery(id+"F2.opFillet","BLEND_EDGE",EDGE,{"blendedFrom":[makeQuery(id+"F1.opExtrude","SWEPT_EDGE",EDGE,{"disambiguationData":[OSD([sQuery(id+"F0.wireOp",EDGE,"E1.bottom"),subQ0])]}),makeQuery(id+"F1.opExtrude","CAP_EDGE",EDGE,{"disambiguationData":[OSD([subQ0])],"isStart":false})],"blendedInto":[]});}
            var Q65;
            Q65=makeQuery(id+"F2.opFillet","BLEND_EDGE",EDGE,{"blendedFrom":[makeQuery(id+"F1.opExtrude","CAP_EDGE",EDGE,{"disambiguationData":[OSD([sQuery(id+"F0.wireOp",EDGE,"E0.bottom"),sQuery(id+"F0.wireOp",EDGE,"E1.bottom")])],"isStart":true}),makeQuery(id+"F1.opExtrude","CAP_EDGE",EDGE,{"disambiguationData":[OSD([sQuery(id+"F0.wireOp",EDGE,"E0.left")])],"isStart":true})],"blendedInto":[]});
            var Q66;
            {var subQ0=sQuery(id+"F0.wireOp",EDGE,"E1.bottom");var subQ1=sQuery(id+"F0.wireOp",EDGE,"E0.bottom");Q66=makeQuery(id+"F2.opFillet","BLEND_EDGE",EDGE,{"blendedFrom":[makeQuery(id+"F1.opExtrude","CAP_EDGE",EDGE,{"disambiguationData":[OSD([subQ1,subQ0])],"isStart":true}),makeQuery(id+"F1.opExtrude","CAP_FACE",FACE,{"disambiguationData":[OSD([subQ1,sQuery(id+"F0.wireOp",EDGE,"E0.top"),sQuery(id+"F0.wireOp",EDGE,"E0.left"),subQ0,sQuery(id+"F0.wireOp",EDGE,"E1.top"),sQuery(id+"F0.wireOp",EDGE,"E1.left"),sQuery(id+"F0.wireOp",EDGE,"E1.right"),sQuery(id+"F0.wireOp",EDGE,"E2.bottom"),sQuery(id+"F0.wireOp",EDGE,"E2.top"),sQuery(id+"F0.wireOp",EDGE,"E2.left")])],"isStart":true})],"blendedInto":[makeQuery(id+"F1.opExtrude","CAP_FACE",FACE,{"disambiguationData":[OSD([subQ1,sQuery(id+"F0.wireOp",EDGE,"E0.top"),sQuery(id+"F0.wireOp",EDGE,"E0.left"),subQ0,sQuery(id+"F0.wireOp",EDGE,"E1.top"),sQuery(id+"F0.wireOp",EDGE,"E1.left"),sQuery(id+"F0.wireOp",EDGE,"E1.right"),sQuery(id+"F0.wireOp",EDGE,"E2.bottom"),sQuery(id+"F0.wireOp",EDGE,"E2.top"),sQuery(id+"F0.wireOp",EDGE,"E2.left")])],"isStart":true})]});}
            var Q67;
            {var subQ0=sQuery(id+"F0.wireOp",EDGE,"E2.left");Q67=makeQuery(id+"F2.opFillet","BLEND_EDGE",EDGE,{"blendedFrom":[makeQuery(id+"F1.opExtrude","CAP_EDGE",EDGE,{"disambiguationData":[OSD([subQ0])],"isStart":true}),makeQuery(id+"F1.opExtrude","SWEPT_FACE",FACE,{"disambiguationData":[OSD([subQ0])]})],"blendedInto":[makeQuery(id+"F1.opExtrude","SWEPT_FACE",FACE,{"disambiguationData":[OSD([subQ0])]})]});}
            var Q68;
            {var subQ0=sQuery(id+"F0.wireOp",EDGE,"E1.bottom");Q68=makeQuery(id+"F2.opFillet","BLEND_EDGE",EDGE,{"blendedFrom":[makeQuery(id+"F1.opExtrude","SWEPT_EDGE",EDGE,{"disambiguationData":[OSD([subQ0,sQuery(id+"F0.wireOp",EDGE,"E1.right")])]}),makeQuery(id+"F1.opExtrude","SWEPT_FACE",FACE,{"disambiguationData":[OSD([sQuery(id+"F0.wireOp",EDGE,"E0.bottom"),subQ0])]})],"blendedInto":[makeQuery(id+"F1.opExtrude","SWEPT_FACE",FACE,{"disambiguationData":[OSD([sQuery(id+"F0.wireOp",EDGE,"E0.bottom"),subQ0])]})]});}
            var Q69;
            {var subQ0=sQuery(id+"F0.wireOp",EDGE,"E2.left");Q69=makeQuery(id+"F2.opFillet","BLEND_EDGE",EDGE,{"blendedFrom":[makeQuery(id+"F1.opExtrude","SWEPT_EDGE",EDGE,{"disambiguationData":[OSD([sQuery(id+"F0.wireOp",EDGE,"E2.top"),subQ0])]}),makeQuery(id+"F1.opExtrude","SWEPT_FACE",FACE,{"disambiguationData":[OSD([subQ0])]})],"blendedInto":[makeQuery(id+"F1.opExtrude","SWEPT_FACE",FACE,{"disambiguationData":[OSD([subQ0])]})]});}
            var Q70;
            {var subQ0=sQuery(id+"F0.wireOp",EDGE,"E2.top");Q70=makeQuery(id+"F2.opFillet","BLEND_EDGE",EDGE,{"blendedFrom":[makeQuery(id+"F1.opExtrude","CAP_VERTEX",VERTEX,{"disambiguationData":[OSD([subQ0,sQuery(id+"F0.wireOp",EDGE,"E2.left")])],"isStart":true}),makeQuery(id+"F1.opExtrude","CAP_EDGE",EDGE,{"disambiguationData":[OSD([sQuery(id+"F0.wireOp",EDGE,"E1.top"),subQ0])],"isStart":true})],"blendedInto":[]});}
            var Q71;
            {var subQ0=sQuery(id+"F0.wireOp",EDGE,"E2.left");var subQ1=sQuery(id+"F0.wireOp",EDGE,"E2.bottom");Q71=makeQuery(id+"F2.opFillet","BLEND_EDGE",EDGE,{"blendedFrom":[makeQuery(id+"F1.opExtrude","CAP_VERTEX",VERTEX,{"disambiguationData":[OSD([subQ1,subQ0])],"isStart":true}),makeQuery(id+"F1.opExtrude","SWEPT_EDGE",EDGE,{"disambiguationData":[OSD([subQ1,subQ0])]})],"blendedInto":[]});}
            var Q72;
            {var subQ0=sQuery(id+"F0.wireOp",EDGE,"E2.left");Q72=makeQuery(id+"F2.opFillet","BLEND_EDGE",EDGE,{"blendedFrom":[makeQuery(id+"F1.opExtrude","CAP_VERTEX",VERTEX,{"disambiguationData":[OSD([sQuery(id+"F0.wireOp",EDGE,"E2.top"),subQ0])],"isStart":true}),makeQuery(id+"F1.opExtrude","CAP_EDGE",EDGE,{"disambiguationData":[OSD([subQ0])],"isStart":true})],"blendedInto":[]});}
            var Q73;
            {var subQ0=sQuery(id+"F0.wireOp",EDGE,"E1.bottom");Q73=makeQuery(id+"F2.opFillet","BLEND_EDGE",EDGE,{"blendedFrom":[makeQuery(id+"F1.opExtrude","CAP_VERTEX",VERTEX,{"disambiguationData":[OSD([subQ0,sQuery(id+"F0.wireOp",EDGE,"E1.right")])],"isStart":true}),makeQuery(id+"F1.opExtrude","CAP_EDGE",EDGE,{"disambiguationData":[OSD([sQuery(id+"F0.wireOp",EDGE,"E0.bottom"),subQ0])],"isStart":true})],"blendedInto":[]});}
            var Q74;
            {var subQ0=sQuery(id+"F0.wireOp",EDGE,"E1.right");Q74=makeQuery(id+"F2.opFillet","BLEND_EDGE",EDGE,{"blendedFrom":[makeQuery(id+"F1.opExtrude","SWEPT_EDGE",EDGE,{"disambiguationData":[OSD([sQuery(id+"F0.wireOp",EDGE,"E1.bottom"),subQ0])]}),makeQuery(id+"F1.opExtrude","SWEPT_FACE",FACE,{"disambiguationData":[OSD([subQ0])]})],"blendedInto":[makeQuery(id+"F1.opExtrude","SWEPT_FACE",FACE,{"disambiguationData":[OSD([subQ0])]})]});}
            var Q75;
            {var subQ0=sQuery(id+"F0.wireOp",EDGE,"E2.left");Q75=makeQuery(id+"F2.opFillet","BLEND_EDGE",EDGE,{"blendedFrom":[makeQuery(id+"F1.opExtrude","CAP_EDGE",EDGE,{"disambiguationData":[OSD([subQ0])],"isStart":true}),makeQuery(id+"F1.opExtrude","CAP_FACE",FACE,{"disambiguationData":[OSD([sQuery(id+"F0.wireOp",EDGE,"E0.bottom"),sQuery(id+"F0.wireOp",EDGE,"E0.top"),sQuery(id+"F0.wireOp",EDGE,"E0.left"),sQuery(id+"F0.wireOp",EDGE,"E1.bottom"),sQuery(id+"F0.wireOp",EDGE,"E1.top"),sQuery(id+"F0.wireOp",EDGE,"E1.left"),sQuery(id+"F0.wireOp",EDGE,"E1.right"),sQuery(id+"F0.wireOp",EDGE,"E2.bottom"),sQuery(id+"F0.wireOp",EDGE,"E2.top"),subQ0])],"isStart":true})],"blendedInto":[makeQuery(id+"F1.opExtrude","CAP_FACE",FACE,{"disambiguationData":[OSD([sQuery(id+"F0.wireOp",EDGE,"E0.bottom"),sQuery(id+"F0.wireOp",EDGE,"E0.top"),sQuery(id+"F0.wireOp",EDGE,"E0.left"),sQuery(id+"F0.wireOp",EDGE,"E1.bottom"),sQuery(id+"F0.wireOp",EDGE,"E1.top"),sQuery(id+"F0.wireOp",EDGE,"E1.left"),sQuery(id+"F0.wireOp",EDGE,"E1.right"),sQuery(id+"F0.wireOp",EDGE,"E2.bottom"),sQuery(id+"F0.wireOp",EDGE,"E2.top"),subQ0])],"isStart":true})]});}
            var Q76;
            {var subQ0=sQuery(id+"F0.wireOp",EDGE,"E2.left");Q76=makeQuery(id+"F2.opFillet","BLEND_EDGE",EDGE,{"blendedFrom":[makeQuery(id+"F1.opExtrude","CAP_VERTEX",VERTEX,{"disambiguationData":[OSD([sQuery(id+"F0.wireOp",EDGE,"E2.bottom"),subQ0])],"isStart":true}),makeQuery(id+"F1.opExtrude","CAP_EDGE",EDGE,{"disambiguationData":[OSD([subQ0])],"isStart":true})],"blendedInto":[]});}
            var Q77;
            {var subQ0=sQuery(id+"F0.wireOp",EDGE,"E2.left");var subQ1=sQuery(id+"F0.wireOp",EDGE,"E2.top");Q77=makeQuery(id+"F2.opFillet","BLEND_EDGE",EDGE,{"blendedFrom":[makeQuery(id+"F1.opExtrude","CAP_VERTEX",VERTEX,{"disambiguationData":[OSD([subQ1,subQ0])],"isStart":true}),makeQuery(id+"F1.opExtrude","SWEPT_EDGE",EDGE,{"disambiguationData":[OSD([subQ1,subQ0])]})],"blendedInto":[]});}
            var Q78;
            {var subQ0=sQuery(id+"F0.wireOp",EDGE,"E2.bottom");Q78=makeQuery(id+"F2.opFillet","BLEND_EDGE",EDGE,{"blendedFrom":[makeQuery(id+"F1.opExtrude","CAP_VERTEX",VERTEX,{"disambiguationData":[OSD([subQ0,sQuery(id+"F0.wireOp",EDGE,"E2.left")])],"isStart":true}),makeQuery(id+"F1.opExtrude","CAP_EDGE",EDGE,{"disambiguationData":[OSD([subQ0])],"isStart":true})],"blendedInto":[]});}
            var Q79;
            {var subQ0=sQuery(id+"F0.wireOp",EDGE,"E1.right");var subQ1=sQuery(id+"F0.wireOp",EDGE,"E1.bottom");Q79=makeQuery(id+"F2.opFillet","BLEND_EDGE",EDGE,{"blendedFrom":[makeQuery(id+"F1.opExtrude","CAP_VERTEX",VERTEX,{"disambiguationData":[OSD([subQ1,subQ0])],"isStart":true}),makeQuery(id+"F1.opExtrude","SWEPT_EDGE",EDGE,{"disambiguationData":[OSD([subQ1,subQ0])]})],"blendedInto":[]});}
            var Q80;
            {var subQ0=sQuery(id+"F0.wireOp",EDGE,"E1.right");Q80=makeQuery(id+"F2.opFillet","BLEND_EDGE",EDGE,{"blendedFrom":[makeQuery(id+"F1.opExtrude","CAP_VERTEX",VERTEX,{"disambiguationData":[OSD([sQuery(id+"F0.wireOp",EDGE,"E1.bottom"),subQ0])],"isStart":true}),makeQuery(id+"F1.opExtrude","CAP_EDGE",EDGE,{"disambiguationData":[OSD([subQ0])],"isStart":true})],"blendedInto":[]});}
            fillet(context, id + "F4", {"entities" : qUnion([Q0, Q1, Q2, Q3, Q4, Q5, Q6, Q7, Q8, Q9, Q10, Q11, Q12, Q13, Q14, Q15, Q16, Q17, Q18, Q19, Q20, Q21, Q22, Q23, Q24, Q25, Q26, Q27, Q28, Q29, Q30, Q31, Q32, Q33, Q34, Q35, Q36, Q37, Q38, Q39, Q40, Q41, Q42, Q43, Q44, Q45, Q46, Q47, Q48, Q49, Q50, Q51, Q52, Q53, Q54, Q55, Q56, Q57, Q58, Q59, Q60, Q61, Q62, Q63, Q64, Q65, Q66, Q67, Q68, Q69, Q70, Q71, Q72, Q73, Q74, Q75, Q76, Q77, Q78, Q79, Q80]), "radius" : 5.08 * mm, "tangentPropagation" : true, "allowEdgeOverflow" : false});
        }
    });
